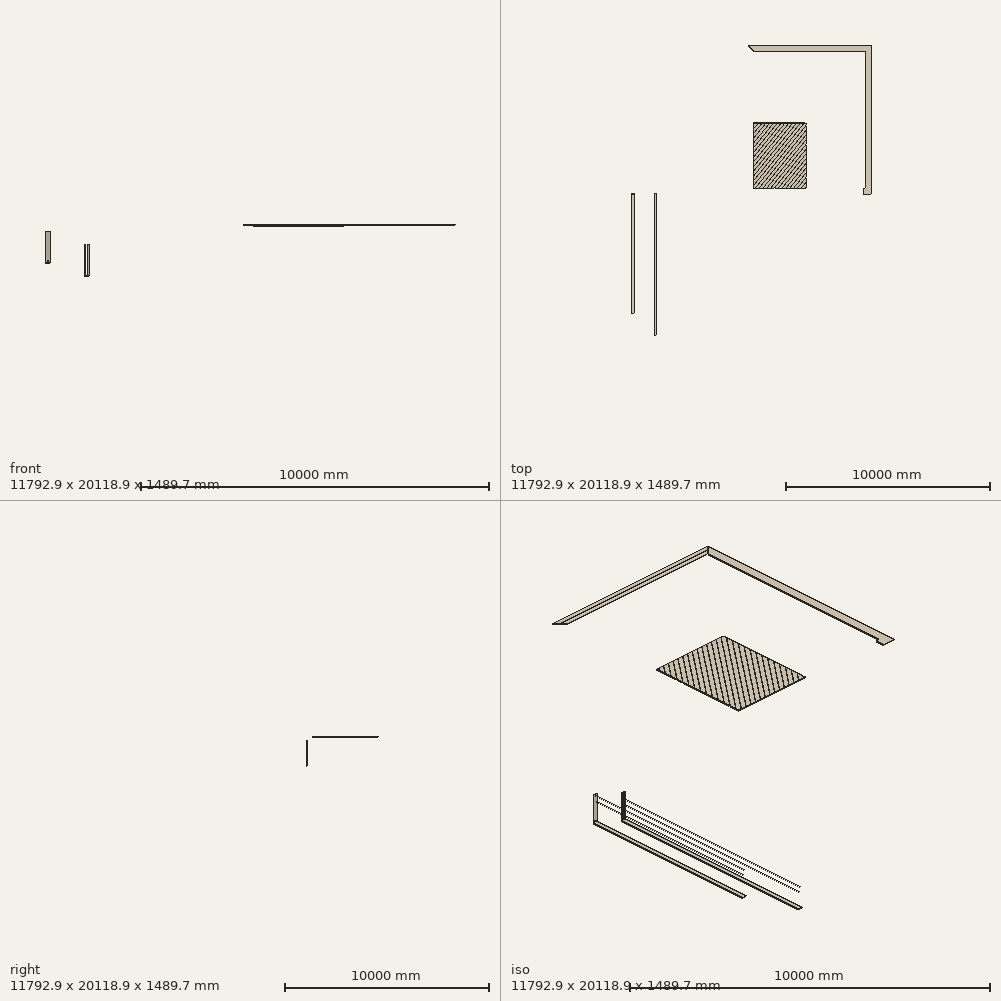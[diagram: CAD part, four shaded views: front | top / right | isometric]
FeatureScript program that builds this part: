
annotation { "Feature Type Name" : "Feature", "Feature Type Description" : "" }
export const myFeature = defineFeature(function(context is Context, id is Id, definition is map)
    precondition{}
    {
        {
            var Q0;
            Q0=qCreatedBy(makeId("Top.planeOp"),FACE);
            var sketch = newSketch(context, id + "F0", { "sketchPlane" : qUnion([Q0])});
            skLineSegment(sketch, "E0.bottom", {"start": v(-394.36, 7277.55) * mm, "end": v(5692.66, 7277.55) * mm});
            skLineSegment(sketch, "E0.top", {"start": v(-398.85, -37.65) * mm, "end": v(5697.15, -37.65) * mm});
            skLineSegment(sketch, "E0.left", {"start": v(-398.85, 7277.55) * mm, "end": v(-398.85, 254.45) * mm});
            skLineSegment(sketch, "E0.right", {"start": v(5697.15, 7273.06) * mm, "end": v(5697.15, -37.65) * mm});
            skLineSegment(sketch, "E1.bottom", {"start": v(5692.66, 7277.55) * mm, "end": v(5290.75, 7277.55) * mm});
            skLineSegment(sketch, "E1.left", {"start": v(5697.15, 7273.06) * mm, "end": v(5697.15, 6871.15) * mm});
            skLineSegment(sketch, "E1.right", {"start": v(5290.75, 6991.8) * mm, "end": v(5290.75, 6871.15) * mm});
            skLineSegment(sketch, "E2.bottom", {"start": v(-394.36, 7277.55) * mm, "end": v(7.55, 7277.55) * mm});
            skLineSegment(sketch, "E2.top", {"start": v(-398.85, 6871.15) * mm, "end": v(7.55, 6871.15) * mm});
            skLineSegment(sketch, "E2.left", {"start": v(-398.85, 7277.55) * mm, "end": v(-398.85, 6871.15) * mm});
            skLineSegment(sketch, "E3.left", {"start": v(5697.15, -37.65) * mm, "end": v(5697.15, 368.75) * mm});
            skLineSegment(sketch, "E3.right", {"start": v(5290.75, -37.65) * mm, "end": v(5290.75, 368.75) * mm});
            skLineSegment(sketch, "E4.bottom", {"start": v(-398.85, -37.65) * mm, "end": v(7.55, -37.65) * mm});
            skLineSegment(sketch, "E4.left", {"start": v(-398.85, 254.45) * mm, "end": v(-398.85, 368.75) * mm});
            skLineSegment(sketch, "E5", {"start": v(-398.85, 7277.55) * mm, "end": v(-259.15, 7137.85) * mm});
            skLineSegment(sketch, "E6.0", {"start": v(-398.85, 7137.85) * mm, "end": v(-259.15, 7137.85) * mm});
            skLineSegment(sketch, "E7.0", {"start": v(5557.45, 7116.26) * mm, "end": v(5557.45, 106.54) * mm});
            skLineSegment(sketch, "E8.0", {"start": v(-398.85, 7131.5) * mm, "end": v(-252.8, 7131.5) * mm});
            skLineSegment(sketch, "E9.0", {"start": v(-398.85, 6991.8) * mm, "end": v(-113.1, 6991.8) * mm});
            skLineSegment(sketch, "E10.trimOffspring", {"start": v(5411.4, 6987.31) * mm, "end": v(5411.4, 252.6) * mm});
            skLineSegment(sketch, "E11.trimOffspring", {"start": v(5551.1, 7116.26) * mm, "end": v(5551.1, 112.9) * mm});
            skLineSegment(sketch, "E12.trimOffspring", {"start": v(5411.4, 6871.15) * mm, "end": v(5290.75, 6871.15) * mm});
            skLineSegment(sketch, "E13.0", {"start": v(5692.66, 7277.55) * mm, "end": v(5552.96, 7137.85) * mm});
            skLineSegment(sketch, "E14.0", {"start": v(5697.15, 7273.06) * mm, "end": v(5557.45, 7133.36) * mm});
            skLineSegment(sketch, "E15.trimOffspring", {"start": v(5290.75, 6875.64) * mm, "end": v(5288.5, 6873.4) * mm});
            skLineSegment(sketch, "E16.trimOffspring", {"start": v(5295.24, 6871.15) * mm, "end": v(5293, 6868.9) * mm});
            skLineSegment(sketch, "E17.trimOffspring", {"start": v(5546.6, 7131.5) * mm, "end": v(5406.9, 6991.8) * mm});
            skLineSegment(sketch, "E18.trimOffspring", {"start": v(5551.1, 7127.01) * mm, "end": v(5411.4, 6987.31) * mm});
            skLineSegment(sketch, "E19.0", {"start": v(-394.36, 7277.55) * mm, "end": v(-254.66, 7137.85) * mm});
            skLineSegment(sketch, "E20.trimOffspring", {"start": v(-248.31, 7131.5) * mm, "end": v(-108.61, 6991.8) * mm});
            skLineSegment(sketch, "E21.trimOffspring", {"start": v(-252.8, 7131.5) * mm, "end": v(7.55, 6871.15) * mm});
            skLineSegment(sketch, "E22.trimOffspring", {"start": v(-254.66, 7137.85) * mm, "end": v(5536.98, 7137.85) * mm});
            skLineSegment(sketch, "E23.trimOffspring", {"start": v(-248.31, 7131.5) * mm, "end": v(5536.98, 7131.5) * mm});
            skLineSegment(sketch, "E24.trimOffspring", {"start": v(-108.61, 6991.8) * mm, "end": v(5406.9, 6991.8) * mm});
            skLineSegment(sketch, "E25.trimOffspring", {"start": v(7.55, 6875.64) * mm, "end": v(7.55, 6871.15) * mm});
            skLineSegment(sketch, "E26.trimOffspring", {"start": v(7.55, 6875.64) * mm, "end": v(9.8, 6873.4) * mm});
            skLineSegment(sketch, "E27.0", {"start": v(5697.15, -33.16) * mm, "end": v(5557.45, 106.54) * mm});
            skLineSegment(sketch, "E28.trimOffspring", {"start": v(5551.1, 112.9) * mm, "end": v(5411.4, 252.6) * mm});
            skLineSegment(sketch, "E29", {"start": v(5546.6, 7131.5) * mm, "end": v(5551.1, 7127.01) * mm});
            skLineSegment(sketch, "E30", {"start": v(5557.45, 7133.36) * mm, "end": v(5552.96, 7137.85) * mm});
            skLineSegment(sketch, "E31", {"start": v(5536.98, 7137.85) * mm, "end": v(5536.98, 7131.5) * mm});
            skLineSegment(sketch, "E32", {"start": v(5551.1, 7116.26) * mm, "end": v(5557.45, 7116.26) * mm});
            skPoint(sketch, "E33.orphan", {"position": v(5546.6, 7137.85) * mm});
            skLineSegment(sketch, "E34", {"start": v(5692.66, 7277.55) * mm, "end": v(5703.74, 7277.55) * mm});
            skLineSegment(sketch, "E35", {"start": v(5697.15, 7273.06) * mm, "end": v(5697.15, 7281.54) * mm});
            skLineSegment(sketch, "E36.0", {"start": v(-106.75, 254.45) * mm, "end": v(-16.83, 254.45) * mm});
            skLineSegment(sketch, "E37.0", {"start": v(-106.75, 7137.85) * mm, "end": v(-106.75, 7131.5) * mm});
            skLineSegment(sketch, "E38.trimOffspring", {"start": v(-106.75, 6991.8) * mm, "end": v(-106.75, 6871.15) * mm});
            skLineSegment(sketch, "E39.trimOffspring", {"start": v(5551.1, 254.45) * mm, "end": v(5557.45, 254.45) * mm});
            skLineSegment(sketch, "E40", {"start": v(2506.27, 254.45) * mm, "end": v(2506.27, 3473.9) * mm});
            skLineSegment(sketch, "E41", {"start": v(-106.75, 3477.08) * mm, "end": v(1529.62, 3477.08) * mm});
            skLineSegment(sketch, "E42.0", {"start": v(-16.83, 254.45) * mm, "end": v(2506.27, 3366.17) * mm});
            skLineSegment(sketch, "E43.0", {"start": v(-106.75, 365.36) * mm, "end": v(2416.35, 3477.08) * mm});
            skLineSegment(sketch, "E44.0", {"start": v(-106.75, 375.44) * mm, "end": v(2408.17, 3477.08) * mm});
            skLineSegment(sketch, "E45.0", {"start": v(-274.45, 390.43) * mm, "end": v(-271.21, 394.43) * mm});
            skLineSegment(sketch, "E46.0", {"start": v(-106.75, 607.34) * mm, "end": v(2220.14, 3477.08) * mm});
            skLineSegment(sketch, "E47.0.1.0", {"start": v(-106.75, 829.06) * mm, "end": v(2040.36, 3477.08) * mm});
            skLineSegment(sketch, "E47.0.1.1", {"start": v(-106.75, 839.14) * mm, "end": v(2032.18, 3477.08) * mm});
            skLineSegment(sketch, "E47.0.2.0", {"start": v(-496.25, 580.5) * mm, "end": v(-398.85, 700.62) * mm});
            skLineSegment(sketch, "E47.0.2.1", {"start": v(-501.18, 584.5) * mm, "end": v(-398.85, 710.7) * mm});
            skLineSegment(sketch, "E47.0.3.0", {"start": v(-607.15, 675.55) * mm, "end": v(-398.85, 932.43) * mm});
            skLineSegment(sketch, "E47.0.3.1", {"start": v(-612.08, 679.55) * mm, "end": v(-398.85, 942.51) * mm});
            skLineSegment(sketch, "E47.0.4.0", {"start": v(-718.04, 770.58) * mm, "end": v(-398.85, 1164.24) * mm});
            skLineSegment(sketch, "E47.0.4.1", {"start": v(-722.98, 774.58) * mm, "end": v(-398.85, 1174.32) * mm});
            skLineSegment(sketch, "E47.0.5.0", {"start": v(-828.94, 865.62) * mm, "end": v(-398.85, 1396.05) * mm});
            skLineSegment(sketch, "E47.0.5.1", {"start": v(-833.87, 869.62) * mm, "end": v(-398.85, 1406.13) * mm});
            skLineSegment(sketch, "E47.0.6.0", {"start": v(-939.84, 960.66) * mm, "end": v(-398.85, 1627.85) * mm});
            skLineSegment(sketch, "E47.0.6.1", {"start": v(-944.77, 964.66) * mm, "end": v(-398.85, 1637.94) * mm});
            skLineSegment(sketch, "E47.0.7.0", {"start": v(-1050.74, 1055.7) * mm, "end": v(-398.85, 1859.66) * mm});
            skLineSegment(sketch, "E47.0.7.1", {"start": v(-1055.67, 1059.7) * mm, "end": v(-398.85, 1869.74) * mm});
            skLineSegment(sketch, "E47.0.8.0", {"start": v(-1161.63, 1150.74) * mm, "end": v(-398.85, 2091.47) * mm});
            skLineSegment(sketch, "E47.0.8.1", {"start": v(-1166.57, 1154.74) * mm, "end": v(-398.85, 2101.55) * mm});
            skLineSegment(sketch, "E47.0.9.0", {"start": v(-1272.53, 1245.78) * mm, "end": v(-398.85, 2323.28) * mm});
            skLineSegment(sketch, "E47.0.9.1", {"start": v(-1277.46, 1249.78) * mm, "end": v(-398.85, 2333.36) * mm});
            skLineSegment(sketch, "E47.0.10.0", {"start": v(-1383.43, 1340.81) * mm, "end": v(-398.85, 2555.09) * mm});
            skLineSegment(sketch, "E47.0.10.1", {"start": v(-1388.36, 1344.81) * mm, "end": v(-398.85, 2565.17) * mm});
            skLineSegment(sketch, "E47.0.11.0", {"start": v(-1494.33, 1435.85) * mm, "end": v(-398.85, 2786.9) * mm});
            skLineSegment(sketch, "E47.0.11.1", {"start": v(-1499.26, 1439.85) * mm, "end": v(-398.85, 2796.98) * mm});
            skLineSegment(sketch, "E47.0.12.0", {"start": v(-1605.23, 1530.9) * mm, "end": v(-398.85, 3018.7) * mm});
            skLineSegment(sketch, "E47.0.12.1", {"start": v(-1610.16, 1534.9) * mm, "end": v(-398.85, 3028.78) * mm});
            skLineSegment(sketch, "E47.direction1", {"start": v(-279.39, 394.43) * mm, "end": v(-253.99, 394.43) * mm, "construction": true});
            skLineSegment(sketch, "E47.direction2", {"start": v(-279.39, 394.43) * mm, "end": v(-390.28, 489.47) * mm, "construction": true});
            skLineSegment(sketch, "E48.0", {"start": v(-8.65, 254.45) * mm, "end": v(2506.27, 3356.1) * mm});
            skLineSegment(sketch, "E49.1.0.0", {"start": v(171, 254.45) * mm, "end": v(2506.27, 3134.52) * mm});
            skLineSegment(sketch, "E49.1.0.1", {"start": v(179.18, 254.45) * mm, "end": v(2506.27, 3124.44) * mm});
            skLineSegment(sketch, "E49.2.0.0", {"start": v(358.83, 254.45) * mm, "end": v(2506.27, 2902.87) * mm});
            skLineSegment(sketch, "E49.2.0.1", {"start": v(367, 254.45) * mm, "end": v(2506.27, 2892.8) * mm});
            skLineSegment(sketch, "E49.3.0.0", {"start": v(274.82, -80.8) * mm, "end": v(309.82, -37.65) * mm});
            skLineSegment(sketch, "E49.3.0.1", {"start": v(279.75, -84.8) * mm, "end": v(318, -37.65) * mm});
            skLineSegment(sketch, "E49.4.0.0", {"start": v(383.93, -177.9) * mm, "end": v(497.65, -37.65) * mm});
            skLineSegment(sketch, "E49.4.0.1", {"start": v(388.86, -181.9) * mm, "end": v(505.82, -37.65) * mm});
            skLineSegment(sketch, "E49.5.0.0", {"start": v(493.04, -274.99) * mm, "end": v(685.48, -37.65) * mm});
            skLineSegment(sketch, "E49.5.0.1", {"start": v(497.97, -278.99) * mm, "end": v(693.65, -37.65) * mm});
            skLineSegment(sketch, "E49.6.0.0", {"start": v(602.14, -372.08) * mm, "end": v(873.3, -37.65) * mm});
            skLineSegment(sketch, "E49.6.0.1", {"start": v(607.07, -376.07) * mm, "end": v(881.48, -37.65) * mm});
            skLineSegment(sketch, "E49.7.0.0", {"start": v(711.25, -469.17) * mm, "end": v(1061.14, -37.65) * mm});
            skLineSegment(sketch, "E49.7.0.1", {"start": v(716.18, -473.16) * mm, "end": v(1069.31, -37.65) * mm});
            skLineSegment(sketch, "E49.8.0.0", {"start": v(820.35, -566.25) * mm, "end": v(1248.97, -37.65) * mm});
            skLineSegment(sketch, "E49.8.0.1", {"start": v(825.29, -570.25) * mm, "end": v(1257.15, -37.65) * mm});
            skLineSegment(sketch, "E49.9.0.0", {"start": v(929.46, -663.34) * mm, "end": v(1436.8, -37.65) * mm});
            skLineSegment(sketch, "E49.9.0.1", {"start": v(934.4, -667.34) * mm, "end": v(1444.98, -37.65) * mm});
            skLineSegment(sketch, "E49.10.0.0", {"start": v(1038.57, -760.43) * mm, "end": v(1624.63, -37.65) * mm});
            skLineSegment(sketch, "E49.10.0.1", {"start": v(1043.5, -764.43) * mm, "end": v(1632.8, -37.65) * mm});
            skLineSegment(sketch, "E49.11.0.0", {"start": v(1147.67, -857.52) * mm, "end": v(1812.46, -37.65) * mm});
            skLineSegment(sketch, "E49.11.0.1", {"start": v(1152.6, -861.52) * mm, "end": v(1820.64, -37.65) * mm});
            skLineSegment(sketch, "E49.12.0.0", {"start": v(1256.78, -954.61) * mm, "end": v(2000.3, -37.65) * mm});
            skLineSegment(sketch, "E49.12.0.1", {"start": v(1261.71, -958.61) * mm, "end": v(2008.47, -37.65) * mm});
            skLineSegment(sketch, "E49.direction1", {"start": v(-52.5, 210.46) * mm, "end": v(56.6, 113.37) * mm, "construction": true});
            skLineSegment(sketch, "E50.0.13.0", {"start": v(1365.89, -1051.7) * mm, "end": v(2188.12, -37.65) * mm});
            skLineSegment(sketch, "E50.3.13.0", {"start": v(1370.82, -1055.7) * mm, "end": v(2196.3, -37.65) * mm});
            skPoint(sketch, "E51.orphan", {"position": v(3760.7, 2365.1) * mm});
            skPoint(sketch, "E52.orphan", {"position": v(3983.84, 2166.92) * mm});
            skPoint(sketch, "E53.orphan", {"position": v(3978.91, 2170.92) * mm});
            skPoint(sketch, "E54.orphan", {"position": v(3874.74, 2264.01) * mm});
            skPoint(sketch, "E55.orphan", {"position": v(3869.8, 2268.01) * mm});
            skPoint(sketch, "E56.orphan", {"position": v(3765.63, 2361.1) * mm});
            skPoint(sketch, "E57.orphan", {"position": v(3656.53, 2458.2) * mm});
            skPoint(sketch, "E58.orphan", {"position": v(3651.6, 2462.2) * mm});
            skPoint(sketch, "E59.orphan", {"position": v(3547.42, 2555.28) * mm});
            skPoint(sketch, "E60.orphan", {"position": v(3542.49, 2559.28) * mm});
            skPoint(sketch, "E61.orphan", {"position": v(3438.31, 2652.37) * mm});
            skPoint(sketch, "E62.orphan", {"position": v(3433.38, 2656.37) * mm});
            skPoint(sketch, "E63.orphan", {"position": v(3329.2, 2749.46) * mm});
            skPoint(sketch, "E64.orphan", {"position": v(3324.27, 2753.46) * mm});
            skPoint(sketch, "E65.orphan", {"position": v(3220.1, 2846.55) * mm});
            skPoint(sketch, "E66.orphan", {"position": v(3215.17, 2850.55) * mm});
            skPoint(sketch, "E67.orphan", {"position": v(3111, 2943.64) * mm});
            skPoint(sketch, "E68.orphan", {"position": v(3106.06, 2947.64) * mm});
            skPoint(sketch, "E69.orphan", {"position": v(3001.89, 3040.73) * mm});
            skPoint(sketch, "E70.orphan", {"position": v(2996.95, 3044.73) * mm});
            skPoint(sketch, "E71.orphan", {"position": v(2887.85, 3141.82) * mm});
            skPoint(sketch, "E72.orphan", {"position": v(2892.78, 3137.82) * mm});
            skPoint(sketch, "E73.orphan", {"position": v(2778.74, 3238.9) * mm});
            skPoint(sketch, "E74.orphan", {"position": v(2783.67, 3234.9) * mm});
            skPoint(sketch, "E75.orphan", {"position": v(2669.63, 3336) * mm});
            skPoint(sketch, "E76.orphan", {"position": v(2674.57, 3332) * mm});
            skPoint(sketch, "E77.orphan", {"position": v(2565.46, 3429.09) * mm});
            skPoint(sketch, "E78.orphan", {"position": v(2560.53, 3433.09) * mm});
            skPoint(sketch, "E79.orphan", {"position": v(2338.57, 3613.06) * mm});
            skPoint(sketch, "E80.orphan", {"position": v(2333.64, 3617.05) * mm});
            skPoint(sketch, "E81.orphan", {"position": v(2222.74, 3712.1) * mm});
            skPoint(sketch, "E82.orphan", {"position": v(2227.67, 3708.1) * mm});
            skPoint(sketch, "E83.orphan", {"position": v(2111.84, 3807.13) * mm});
            skPoint(sketch, "E84.orphan", {"position": v(2116.78, 3803.13) * mm});
            skPoint(sketch, "E85.orphan", {"position": v(2005.88, 3898.17) * mm});
            skPoint(sketch, "E86.orphan", {"position": v(2000.95, 3902.17) * mm});
            skPoint(sketch, "E87.orphan", {"position": v(1894.98, 3993.2) * mm});
            skPoint(sketch, "E88.orphan", {"position": v(1890.05, 3997.2) * mm});
            skPoint(sketch, "E89.orphan", {"position": v(1784.08, 4088.25) * mm});
            skLineSegment(sketch, "E90", {"start": v(1529.62, 3477.08) * mm, "end": v(2506.27, 3477.08) * mm});
            skPoint(sketch, "E91.orphan", {"position": v(1779.15, 4092.25) * mm});
            skPoint(sketch, "E92.orphan", {"position": v(1673.19, 4183.29) * mm});
            skPoint(sketch, "E93.orphan", {"position": v(1668.25, 4187.29) * mm});
            skPoint(sketch, "E94.orphan", {"position": v(1562.29, 4278.32) * mm});
            skPoint(sketch, "E95.orphan", {"position": v(1557.36, 4282.32) * mm});
            skPoint(sketch, "E96.orphan", {"position": v(1451.4, 4373.36) * mm});
            skPoint(sketch, "E97.orphan", {"position": v(1446.46, 4377.36) * mm});
            skPoint(sketch, "E98.orphan", {"position": v(1340.5, 4468.4) * mm});
            skPoint(sketch, "E99.orphan", {"position": v(1335.56, 4472.4) * mm});
            skPoint(sketch, "E100.orphan", {"position": v(1229.6, 4563.44) * mm});
            skPoint(sketch, "E101.orphan", {"position": v(1224.66, 4567.44) * mm});
            skPoint(sketch, "E102.orphan", {"position": v(1118.7, 4658.48) * mm});
            skPoint(sketch, "E103.orphan", {"position": v(1113.76, 4662.48) * mm});
            skPoint(sketch, "E104.orphan", {"position": v(1007.8, 4753.52) * mm});
            skPoint(sketch, "E105.orphan", {"position": v(1002.87, 4757.52) * mm});
            skLineSegment(sketch, "E106.trimOffspring", {"start": v(-106.75, 3389.03) * mm, "end": v(-35.36, 3477.08) * mm});
            skLineSegment(sketch, "E107.trimOffspring", {"start": v(-106.75, 3378.95) * mm, "end": v(-27.18, 3477.08) * mm});
            skLineSegment(sketch, "E108.trimOffspring", {"start": v(-106.75, 3157.22) * mm, "end": v(152.6, 3477.08) * mm});
            skLineSegment(sketch, "E109.trimOffspring", {"start": v(-106.75, 3147.14) * mm, "end": v(160.77, 3477.08) * mm});
            skLineSegment(sketch, "E110.trimOffspring", {"start": v(-106.75, 2925.41) * mm, "end": v(340.56, 3477.08) * mm});
            skLineSegment(sketch, "E111.trimOffspring", {"start": v(-106.75, 2915.33) * mm, "end": v(348.73, 3477.08) * mm});
            skLineSegment(sketch, "E112.trimOffspring", {"start": v(-106.75, 2693.6) * mm, "end": v(528.52, 3477.08) * mm});
            skLineSegment(sketch, "E113.trimOffspring", {"start": v(-106.75, 2683.52) * mm, "end": v(536.7, 3477.08) * mm});
            skLineSegment(sketch, "E114.trimOffspring", {"start": v(-106.75, 2461.8) * mm, "end": v(716.47, 3477.08) * mm});
            skLineSegment(sketch, "E115.trimOffspring", {"start": v(-106.75, 2451.72) * mm, "end": v(724.65, 3477.08) * mm});
            skLineSegment(sketch, "E116.trimOffspring", {"start": v(-106.75, 2229.99) * mm, "end": v(904.43, 3477.08) * mm});
            skLineSegment(sketch, "E117.trimOffspring", {"start": v(-106.75, 2219.9) * mm, "end": v(912.6, 3477.08) * mm});
            skLineSegment(sketch, "E118.trimOffspring", {"start": v(-106.75, 1998.18) * mm, "end": v(1092.4, 3477.08) * mm});
            skLineSegment(sketch, "E119.trimOffspring", {"start": v(-106.75, 1988.1) * mm, "end": v(1100.57, 3477.08) * mm});
            skLineSegment(sketch, "E120.trimOffspring", {"start": v(-106.75, 1766.37) * mm, "end": v(1280.35, 3477.08) * mm});
            skLineSegment(sketch, "E121.trimOffspring", {"start": v(-106.75, 1756.3) * mm, "end": v(1288.52, 3477.08) * mm});
            skLineSegment(sketch, "E122.trimOffspring", {"start": v(-106.75, 1524.48) * mm, "end": v(1476.48, 3477.08) * mm});
            skLineSegment(sketch, "E123.trimOffspring", {"start": v(-106.75, 1534.57) * mm, "end": v(1468.3, 3477.08) * mm});
            skLineSegment(sketch, "E124.trimOffspring", {"start": v(-106.75, 1302.76) * mm, "end": v(1656.27, 3477.08) * mm});
            skLineSegment(sketch, "E125.trimOffspring", {"start": v(-106.75, 1292.68) * mm, "end": v(1664.44, 3477.08) * mm});
            skLineSegment(sketch, "E126.trimOffspring", {"start": v(-106.75, 1070.95) * mm, "end": v(1844.23, 3477.08) * mm});
            skLineSegment(sketch, "E127.trimOffspring", {"start": v(-106.75, 1060.87) * mm, "end": v(1852.4, 3477.08) * mm});
            skPoint(sketch, "E128.orphan", {"position": v(-385.35, 485.47) * mm});
            skLineSegment(sketch, "E129.trimOffspring", {"start": v(-106.75, 597.25) * mm, "end": v(2228.32, 3477.08) * mm});
            skPoint(sketch, "E130.orphan", {"position": v(-47.57, 206.46) * mm});
            skPoint(sketch, "E131.orphan", {"position": v(61.54, 109.37) * mm});
            skPoint(sketch, "E132.orphan", {"position": v(165.72, 16.28) * mm});
            skPoint(sketch, "E133.orphan", {"position": v(170.65, 12.28) * mm});
            skLineSegment(sketch, "E134.trimOffspring", {"start": v(554.84, 254.45) * mm, "end": v(2506.27, 2661.14) * mm});
            skLineSegment(sketch, "E135.trimOffspring", {"start": v(546.66, 254.45) * mm, "end": v(2506.27, 2671.22) * mm});
            skLineSegment(sketch, "E136.trimOffspring", {"start": v(734.5, 254.45) * mm, "end": v(2506.27, 2439.57) * mm});
            skLineSegment(sketch, "E137.trimOffspring", {"start": v(742.67, 254.45) * mm, "end": v(2506.27, 2429.5) * mm});
            skLineSegment(sketch, "E138.trimOffspring", {"start": v(922.32, 254.45) * mm, "end": v(2506.27, 2207.92) * mm});
            skLineSegment(sketch, "E139.trimOffspring", {"start": v(930.5, 254.45) * mm, "end": v(2506.27, 2197.84) * mm});
            skLineSegment(sketch, "E140.trimOffspring", {"start": v(1110.15, 254.45) * mm, "end": v(2506.27, 1976.27) * mm});
            skLineSegment(sketch, "E141.trimOffspring", {"start": v(1118.33, 254.45) * mm, "end": v(2506.27, 1966.2) * mm});
            skLineSegment(sketch, "E142.trimOffspring", {"start": v(1297.99, 254.45) * mm, "end": v(2506.27, 1744.62) * mm});
            skLineSegment(sketch, "E143.trimOffspring", {"start": v(1306.16, 254.45) * mm, "end": v(2506.27, 1734.54) * mm});
            skLineSegment(sketch, "E144.trimOffspring", {"start": v(1494, 254.45) * mm, "end": v(2506.27, 1502.9) * mm});
            skLineSegment(sketch, "E145.trimOffspring", {"start": v(1485.82, 254.45) * mm, "end": v(2506.27, 1512.97) * mm});
            skLineSegment(sketch, "E146.trimOffspring", {"start": v(1681.82, 254.45) * mm, "end": v(2506.27, 1271.24) * mm});
            skLineSegment(sketch, "E147.trimOffspring", {"start": v(1673.65, 254.45) * mm, "end": v(2506.27, 1281.32) * mm});
            skLineSegment(sketch, "E148.trimOffspring", {"start": v(1869.65, 254.45) * mm, "end": v(2506.27, 1039.6) * mm});
            skLineSegment(sketch, "E149.trimOffspring", {"start": v(1861.48, 254.45) * mm, "end": v(2506.27, 1049.68) * mm});
            skLineSegment(sketch, "E150.trimOffspring", {"start": v(2057.48, 254.45) * mm, "end": v(2506.27, 807.94) * mm});
            skLineSegment(sketch, "E151.trimOffspring", {"start": v(2049.3, 254.45) * mm, "end": v(2506.27, 818.03) * mm});
            skLineSegment(sketch, "E152.trimOffspring", {"start": v(2237.14, 254.45) * mm, "end": v(2506.27, 586.38) * mm});
            skLineSegment(sketch, "E153.trimOffspring", {"start": v(2245.31, 254.45) * mm, "end": v(2506.27, 576.3) * mm});
            skLineSegment(sketch, "E154.trimOffspring", {"start": v(2424.97, 254.45) * mm, "end": v(2506.27, 354.73) * mm});
            skLineSegment(sketch, "E155.trimOffspring", {"start": v(2433.14, 254.45) * mm, "end": v(2506.27, 344.64) * mm});
            skLineSegment(sketch, "E156.0", {"start": v(2509.45, 254.45) * mm, "end": v(2509.45, 3477.08) * mm});
            skLineSegment(sketch, "E157.0", {"start": v(-106.75, 3473.9) * mm, "end": v(1529.62, 3473.9) * mm});
            skLineSegment(sketch, "E158.0", {"start": v(1529.62, 3473.9) * mm, "end": v(2506.27, 3473.9) * mm});
            skLineSegment(sketch, "E159.trimOffspring", {"start": v(2433.14, 254.45) * mm, "end": v(5411.4, 254.45) * mm});
            skLineSegment(sketch, "E160.trimOffspring", {"start": v(2245.31, 254.45) * mm, "end": v(2424.97, 254.45) * mm});
            skLineSegment(sketch, "E161.trimOffspring", {"start": v(1869.65, 254.45) * mm, "end": v(2049.3, 254.45) * mm});
            skLineSegment(sketch, "E162.trimOffspring", {"start": v(1681.82, 254.45) * mm, "end": v(1861.48, 254.45) * mm});
            skLineSegment(sketch, "E163", {"start": v(2057.48, 254.45) * mm, "end": v(2237.14, 254.45) * mm});
            skLineSegment(sketch, "E164.trimOffspring", {"start": v(1494, 254.45) * mm, "end": v(1673.65, 254.45) * mm});
            skLineSegment(sketch, "E165.trimOffspring", {"start": v(1306.16, 254.45) * mm, "end": v(1485.82, 254.45) * mm});
            skLineSegment(sketch, "E166.trimOffspring", {"start": v(1118.33, 254.45) * mm, "end": v(1297.99, 254.45) * mm});
            skLineSegment(sketch, "E167.trimOffspring", {"start": v(930.5, 254.45) * mm, "end": v(1110.15, 254.45) * mm});
            skLineSegment(sketch, "E168.trimOffspring", {"start": v(742.67, 254.45) * mm, "end": v(922.32, 254.45) * mm});
            skLineSegment(sketch, "E169.trimOffspring", {"start": v(554.84, 254.45) * mm, "end": v(734.5, 254.45) * mm});
            skLineSegment(sketch, "E170.trimOffspring", {"start": v(367, 254.45) * mm, "end": v(546.66, 254.45) * mm});
            skLineSegment(sketch, "E171.trimOffspring", {"start": v(179.18, 254.45) * mm, "end": v(358.83, 254.45) * mm});
            skLineSegment(sketch, "E172.trimOffspring", {"start": v(-8.65, 254.45) * mm, "end": v(171, 254.45) * mm});
            skPoint(sketch, "E173.orphan", {"position": v(-106.75, -37.65) * mm});
            skLineSegment(sketch, "E174.trimOffspring", {"start": v(-106.75, 365.36) * mm, "end": v(-106.75, 254.45) * mm});
            skLineSegment(sketch, "E175.trimOffspring", {"start": v(-106.75, 597.25) * mm, "end": v(-106.75, 375.44) * mm});
            skLineSegment(sketch, "E176.trimOffspring", {"start": v(-106.75, 829.06) * mm, "end": v(-106.75, 607.34) * mm});
            skLineSegment(sketch, "E177.trimOffspring", {"start": v(-106.75, 1060.87) * mm, "end": v(-106.75, 839.14) * mm});
            skLineSegment(sketch, "E178.trimOffspring", {"start": v(-106.75, 1292.68) * mm, "end": v(-106.75, 1070.95) * mm});
            skLineSegment(sketch, "E179.trimOffspring", {"start": v(-106.75, 1524.48) * mm, "end": v(-106.75, 1302.76) * mm});
            skLineSegment(sketch, "E180.trimOffspring", {"start": v(-106.75, 1756.3) * mm, "end": v(-106.75, 1534.57) * mm});
            skLineSegment(sketch, "E181.trimOffspring", {"start": v(-106.75, 1988.1) * mm, "end": v(-106.75, 1766.37) * mm});
            skLineSegment(sketch, "E182.trimOffspring", {"start": v(-106.75, 2219.9) * mm, "end": v(-106.75, 1998.18) * mm});
            skLineSegment(sketch, "E183.trimOffspring", {"start": v(-106.75, 2451.72) * mm, "end": v(-106.75, 2229.99) * mm});
            skLineSegment(sketch, "E184.trimOffspring", {"start": v(-106.75, 2683.52) * mm, "end": v(-106.75, 2461.8) * mm});
            skLineSegment(sketch, "E185.trimOffspring", {"start": v(-106.75, 2915.33) * mm, "end": v(-106.75, 2693.6) * mm});
            skLineSegment(sketch, "E186.trimOffspring", {"start": v(-106.75, 3147.14) * mm, "end": v(-106.75, 2925.41) * mm});
            skLineSegment(sketch, "E187.trimOffspring", {"start": v(-106.75, 3378.95) * mm, "end": v(-106.75, 3157.22) * mm});
            skLineSegment(sketch, "E188.trimOffspring", {"start": v(-106.75, 3477.08) * mm, "end": v(-106.75, 3389.03) * mm});
            skLineSegment(sketch, "E189", {"start": v(2506.27, 3477.08) * mm, "end": v(2509.45, 3477.08) * mm});
            skPoint(sketch, "E190.orphan", {"position": v(2506.27, 4118.32) * mm});
            skLineSegment(sketch, "E191.0", {"start": v(2433.14, 111.58) * mm, "end": v(5411.4, 111.58) * mm});
            skSolve(sketch);
        }
        {
            var Q0;
            {var subQ3=sQuery(id+"F0.wireOp",EDGE,"E17.trimOffspring");Q0=makeQuery(id+"F0.imprint","IMPRINT",FACE,{"disambiguationData":[TD([[makeQuery(id+"F0.imprint","IMPRINT",EDGE,{"derivedFrom":subQ3}),-1.0]])]});}
            var Q1;
            Q1=makeQuery(id+"F0.imprint","IMPRINT",FACE,{"disambiguationData":[TD([[makeQuery(id+"F0.imprint","IMPRINT",EDGE,{"derivedFrom":sQuery(id+"F0.wireOp",EDGE,"E0.bottom")}),-1.0]])]});
            var Q2;
            {var subQ1=sQuery(id+"F0.wireOp",EDGE,"E0.right");Q2=makeQuery(id+"F0.imprint","IMPRINT",FACE,{"disambiguationData":[TD([[makeQuery(id+"F0.imprint","IMPRINT",EDGE,{"derivedFrom":subQ1}),-1.0]])]});}
            var Q3;
            Q3=makeQuery(id+"F0.imprint","IMPRINT",FACE,{"disambiguationData":[TD([[makeQuery(id+"F0.imprint","IMPRINT",EDGE,{"derivedFrom":sQuery(id+"F0.wireOp",EDGE,"E11.trimOffspring")}),-1.0]])]});
            extrude(context, id + "F1", {"entities" : qUnion([Q0, Q1, Q2, Q3]), "depth" : 25.4 * mm});
        }
        {
            var Q0;
            Q0=makeQuery(id+"F1.opExtrude","CAP_FACE",FACE,{"disambiguationData":[OSD([sQuery(id+"F0.wireOp",EDGE,"E0.bottom"),sQuery(id+"F0.wireOp",EDGE,"E0.right"),sQuery(id+"F0.wireOp",EDGE,"E1.bottom"),sQuery(id+"F0.wireOp",EDGE,"E1.left"),sQuery(id+"F0.wireOp",EDGE,"E2.bottom"),sQuery(id+"F0.wireOp",EDGE,"E3.left"),sQuery(id+"F0.wireOp",EDGE,"E7.0"),sQuery(id+"F0.wireOp",EDGE,"E10.trimOffspring"),sQuery(id+"F0.wireOp",EDGE,"E11.trimOffspring"),sQuery(id+"F0.wireOp",EDGE,"E13.0"),sQuery(id+"F0.wireOp",EDGE,"E14.0"),sQuery(id+"F0.wireOp",EDGE,"E17.trimOffspring"),sQuery(id+"F0.wireOp",EDGE,"E18.trimOffspring"),sQuery(id+"F0.wireOp",EDGE,"E19.0"),sQuery(id+"F0.wireOp",EDGE,"E20.trimOffspring"),sQuery(id+"F0.wireOp",EDGE,"E22.trimOffspring"),sQuery(id+"F0.wireOp",EDGE,"E23.trimOffspring"),sQuery(id+"F0.wireOp",EDGE,"E24.trimOffspring"),sQuery(id+"F0.wireOp",EDGE,"E27.0"),sQuery(id+"F0.wireOp",EDGE,"E28.trimOffspring"),sQuery(id+"F0.wireOp",EDGE,"E29"),sQuery(id+"F0.wireOp",EDGE,"E30"),sQuery(id+"F0.wireOp",EDGE,"E31"),sQuery(id+"F0.wireOp",EDGE,"E32")])],"isStart":false});
            extrude(context, id + "F2", {"entities" : qUnion([Q0]), "depth" : 25.4 * mm});
        }
        {
            var Q0;
            Q0=makeQuery(id+"F1.opExtrude","SWEPT_BODY",BODY,{"disambiguationData":[OSD([sQuery(id+"F0.wireOp",EDGE,"E0.bottom"),sQuery(id+"F0.wireOp",EDGE,"E0.right"),sQuery(id+"F0.wireOp",EDGE,"E1.bottom"),sQuery(id+"F0.wireOp",EDGE,"E1.left"),sQuery(id+"F0.wireOp",EDGE,"E2.bottom"),sQuery(id+"F0.wireOp",EDGE,"E3.left"),sQuery(id+"F0.wireOp",EDGE,"E7.0"),sQuery(id+"F0.wireOp",EDGE,"E10.trimOffspring"),sQuery(id+"F0.wireOp",EDGE,"E11.trimOffspring"),sQuery(id+"F0.wireOp",EDGE,"E13.0"),sQuery(id+"F0.wireOp",EDGE,"E14.0"),sQuery(id+"F0.wireOp",EDGE,"E17.trimOffspring"),sQuery(id+"F0.wireOp",EDGE,"E18.trimOffspring"),sQuery(id+"F0.wireOp",EDGE,"E19.0"),sQuery(id+"F0.wireOp",EDGE,"E20.trimOffspring"),sQuery(id+"F0.wireOp",EDGE,"E22.trimOffspring"),sQuery(id+"F0.wireOp",EDGE,"E23.trimOffspring"),sQuery(id+"F0.wireOp",EDGE,"E24.trimOffspring"),sQuery(id+"F0.wireOp",EDGE,"E27.0"),sQuery(id+"F0.wireOp",EDGE,"E28.trimOffspring"),sQuery(id+"F0.wireOp",EDGE,"E29"),sQuery(id+"F0.wireOp",EDGE,"E30"),sQuery(id+"F0.wireOp",EDGE,"E31"),sQuery(id+"F0.wireOp",EDGE,"E32")])]});
            deleteBodies(context, id + "F3", {"entities" : qUnion([Q0])});
        }
        {
            var Q0;
            {var subQ0=sQuery(id+"F0.wireOp",EDGE,"E175.trimOffspring");Q0=makeQuery(id+"F0.imprint","IMPRINT",FACE,{"disambiguationData":[TD([[makeQuery(id+"F0.imprint","IMPRINT",EDGE,{"derivedFrom":subQ0}),1.0]])]});}
            var Q1;
            {var subQ0=sQuery(id+"F0.wireOp",EDGE,"E143.trimOffspring");Q1=makeQuery(id+"F0.imprint","IMPRINT",FACE,{"disambiguationData":[TD([[makeQuery(id+"F0.imprint","IMPRINT",EDGE,{"derivedFrom":subQ0}),-1.0]])]});}
            var Q2;
            {var subQ0=sQuery(id+"F0.wireOp",EDGE,"E134.trimOffspring");Q2=makeQuery(id+"F0.imprint","IMPRINT",FACE,{"disambiguationData":[TD([[makeQuery(id+"F0.imprint","IMPRINT",EDGE,{"derivedFrom":subQ0}),-1.0]])]});}
            var Q3;
            {var subQ0=sQuery(id+"F0.wireOp",EDGE,"E186.trimOffspring");Q3=makeQuery(id+"F0.imprint","IMPRINT",FACE,{"disambiguationData":[TD([[makeQuery(id+"F0.imprint","IMPRINT",EDGE,{"derivedFrom":subQ0}),1.0]])]});}
            var Q4;
            {var subQ7=sQuery(id+"F0.wireOp",EDGE,"E179.trimOffspring");Q4=makeQuery(id+"F0.imprint","IMPRINT",FACE,{"disambiguationData":[TD([[makeQuery(id+"F0.imprint","IMPRINT",EDGE,{"derivedFrom":subQ7}),1.0]])]});}
            var Q5;
            {var subQ0=sQuery(id+"F0.wireOp",EDGE,"E153.trimOffspring");Q5=makeQuery(id+"F0.imprint","IMPRINT",FACE,{"disambiguationData":[TD([[makeQuery(id+"F0.imprint","IMPRINT",EDGE,{"derivedFrom":subQ0}),-1.0]])]});}
            var Q6;
            {var subQ0=sQuery(id+"F0.wireOp",EDGE,"E137.trimOffspring");Q6=makeQuery(id+"F0.imprint","IMPRINT",FACE,{"disambiguationData":[TD([[makeQuery(id+"F0.imprint","IMPRINT",EDGE,{"derivedFrom":subQ0}),-1.0]])]});}
            var Q7;
            {var subQ0=sQuery(id+"F0.wireOp",EDGE,"E182.trimOffspring");Q7=makeQuery(id+"F0.imprint","IMPRINT",FACE,{"disambiguationData":[TD([[makeQuery(id+"F0.imprint","IMPRINT",EDGE,{"derivedFrom":subQ0}),1.0]])]});}
            var Q8;
            {var subQ0=sQuery(id+"F0.wireOp",EDGE,"E178.trimOffspring");Q8=makeQuery(id+"F0.imprint","IMPRINT",FACE,{"disambiguationData":[TD([[makeQuery(id+"F0.imprint","IMPRINT",EDGE,{"derivedFrom":subQ0}),1.0]])]});}
            var Q9;
            {var subQ0=sQuery(id+"F0.wireOp",EDGE,"E150.trimOffspring");Q9=makeQuery(id+"F0.imprint","IMPRINT",FACE,{"disambiguationData":[TD([[makeQuery(id+"F0.imprint","IMPRINT",EDGE,{"derivedFrom":subQ0}),-1.0]])]});}
            var Q10;
            {var subQ0=sQuery(id+"F0.wireOp",EDGE,"E184.trimOffspring");Q10=makeQuery(id+"F0.imprint","IMPRINT",FACE,{"disambiguationData":[TD([[makeQuery(id+"F0.imprint","IMPRINT",EDGE,{"derivedFrom":subQ0}),1.0]])]});}
            var Q11;
            {var subQ0=sQuery(id+"F0.wireOp",EDGE,"E139.trimOffspring");Q11=makeQuery(id+"F0.imprint","IMPRINT",FACE,{"disambiguationData":[TD([[makeQuery(id+"F0.imprint","IMPRINT",EDGE,{"derivedFrom":subQ0}),-1.0]])]});}
            var Q12;
            {var subQ0=sQuery(id+"F0.wireOp",EDGE,"E176.trimOffspring");Q12=makeQuery(id+"F0.imprint","IMPRINT",FACE,{"disambiguationData":[TD([[makeQuery(id+"F0.imprint","IMPRINT",EDGE,{"derivedFrom":subQ0}),1.0]])]});}
            var Q13;
            {var subQ0=sQuery(id+"F0.wireOp",EDGE,"E49.2.0.1");Q13=makeQuery(id+"F0.imprint","IMPRINT",FACE,{"disambiguationData":[TD([[makeQuery(id+"F0.imprint","IMPRINT",EDGE,{"derivedFrom":subQ0}),-1.0]])]});}
            var Q14;
            {var subQ0=sQuery(id+"F0.wireOp",EDGE,"E48.0");Q14=makeQuery(id+"F0.imprint","IMPRINT",FACE,{"disambiguationData":[TD([[makeQuery(id+"F0.imprint","IMPRINT",EDGE,{"derivedFrom":subQ0}),-1.0]])]});}
            var Q15;
            {var subQ0=sQuery(id+"F0.wireOp",EDGE,"E185.trimOffspring");Q15=makeQuery(id+"F0.imprint","IMPRINT",FACE,{"disambiguationData":[TD([[makeQuery(id+"F0.imprint","IMPRINT",EDGE,{"derivedFrom":subQ0}),1.0]])]});}
            var Q16;
            {var subQ0=sQuery(id+"F0.wireOp",EDGE,"E181.trimOffspring");Q16=makeQuery(id+"F0.imprint","IMPRINT",FACE,{"disambiguationData":[TD([[makeQuery(id+"F0.imprint","IMPRINT",EDGE,{"derivedFrom":subQ0}),1.0]])]});}
            var Q17;
            {var subQ0=sQuery(id+"F0.wireOp",EDGE,"E183.trimOffspring");Q17=makeQuery(id+"F0.imprint","IMPRINT",FACE,{"disambiguationData":[TD([[makeQuery(id+"F0.imprint","IMPRINT",EDGE,{"derivedFrom":subQ0}),1.0]])]});}
            var Q18;
            {var subQ0=sQuery(id+"F0.wireOp",EDGE,"E180.trimOffspring");Q18=makeQuery(id+"F0.imprint","IMPRINT",FACE,{"disambiguationData":[TD([[makeQuery(id+"F0.imprint","IMPRINT",EDGE,{"derivedFrom":subQ0}),1.0]])]});}
            var Q19;
            {var subQ0=sQuery(id+"F0.wireOp",EDGE,"E141.trimOffspring");Q19=makeQuery(id+"F0.imprint","IMPRINT",FACE,{"disambiguationData":[TD([[makeQuery(id+"F0.imprint","IMPRINT",EDGE,{"derivedFrom":subQ0}),-1.0]])]});}
            var Q20;
            {var subQ0=sQuery(id+"F0.wireOp",EDGE,"E146.trimOffspring");Q20=makeQuery(id+"F0.imprint","IMPRINT",FACE,{"disambiguationData":[TD([[makeQuery(id+"F0.imprint","IMPRINT",EDGE,{"derivedFrom":subQ0}),-1.0]])]});}
            var Q21;
            Q21=makeQuery(id+"F0.imprint","IMPRINT",FACE,{"disambiguationData":[TD([[makeQuery(id+"F0.imprint","IMPRINT",EDGE,{"derivedFrom":sQuery(id+"F0.wireOp",EDGE,"E36.0")}),1.0]])]});
            var Q22;
            {var subQ0=sQuery(id+"F0.wireOp",EDGE,"E148.trimOffspring");Q22=makeQuery(id+"F0.imprint","IMPRINT",FACE,{"disambiguationData":[TD([[makeQuery(id+"F0.imprint","IMPRINT",EDGE,{"derivedFrom":subQ0}),-1.0]])]});}
            var Q23;
            {var subQ0=sQuery(id+"F0.wireOp",EDGE,"E144.trimOffspring");Q23=makeQuery(id+"F0.imprint","IMPRINT",FACE,{"disambiguationData":[TD([[makeQuery(id+"F0.imprint","IMPRINT",EDGE,{"derivedFrom":subQ0}),-1.0]])]});}
            var Q24;
            {var subQ0=sQuery(id+"F0.wireOp",EDGE,"E177.trimOffspring");Q24=makeQuery(id+"F0.imprint","IMPRINT",FACE,{"disambiguationData":[TD([[makeQuery(id+"F0.imprint","IMPRINT",EDGE,{"derivedFrom":subQ0}),1.0]])]});}
            var Q25;
            {var subQ0=sQuery(id+"F0.wireOp",EDGE,"E187.trimOffspring");Q25=makeQuery(id+"F0.imprint","IMPRINT",FACE,{"disambiguationData":[TD([[makeQuery(id+"F0.imprint","IMPRINT",EDGE,{"derivedFrom":subQ0}),1.0]])]});}
            var Q26;
            {var subQ0=sQuery(id+"F0.wireOp",EDGE,"E49.1.0.1");Q26=makeQuery(id+"F0.imprint","IMPRINT",FACE,{"disambiguationData":[TD([[makeQuery(id+"F0.imprint","IMPRINT",EDGE,{"derivedFrom":subQ0}),-1.0]])]});}
            var Q27;
            {var subQ3=sQuery(id+"F0.wireOp",EDGE,"E155.trimOffspring");Q27=makeQuery(id+"F0.imprint","IMPRINT",FACE,{"disambiguationData":[TD([[makeQuery(id+"F0.imprint","IMPRINT",EDGE,{"derivedFrom":subQ3}),-1.0]])]});}
            var Q28;
            {var subQ0=sQuery(id+"F0.wireOp",EDGE,"E90");var subQ1=sQuery(id+"F0.wireOp",EDGE,"E47.0.1.1");var subQ2=makeQuery(id+"F0.imprint","INTERSECT",VERTEX,{"derivedFrom":[subQ1,subQ0]});Q28=makeQuery(id+"F0.imprint","IMPRINT",FACE,{"disambiguationData":[TD([[makeQuery(id+"F0.imprint","IMPRINT",EDGE,{"disambiguationData":[TD([[subQ2,1.0]])],"derivedFrom":subQ1}),1.0]])]});}
            var Q29;
            {var subQ0=sQuery(id+"F0.wireOp",EDGE,"E125.trimOffspring");var subQ1=sQuery(id+"F0.wireOp",EDGE,"E90");var subQ2=makeQuery(id+"F0.imprint","INTERSECT",VERTEX,{"derivedFrom":[subQ1,subQ0]});Q29=makeQuery(id+"F0.imprint","IMPRINT",FACE,{"disambiguationData":[TD([[makeQuery(id+"F0.imprint","IMPRINT",EDGE,{"disambiguationData":[TD([[subQ2,-1.0]])],"derivedFrom":subQ1}),-1.0]])]});}
            var Q30;
            {var subQ0=sQuery(id+"F0.wireOp",EDGE,"E90");var subQ1=sQuery(id+"F0.wireOp",EDGE,"E46.0");var subQ2=makeQuery(id+"F0.imprint","INTERSECT",VERTEX,{"derivedFrom":[subQ1,subQ0]});Q30=makeQuery(id+"F0.imprint","IMPRINT",FACE,{"disambiguationData":[TD([[makeQuery(id+"F0.imprint","IMPRINT",EDGE,{"disambiguationData":[TD([[subQ2,1.0]])],"derivedFrom":subQ1}),1.0]])]});}
            var Q31;
            {var subQ0=sQuery(id+"F0.wireOp",EDGE,"E117.trimOffspring");var subQ1=sQuery(id+"F0.wireOp",EDGE,"E41");var subQ2=makeQuery(id+"F0.imprint","INTERSECT",VERTEX,{"derivedFrom":[subQ1,subQ0]});Q31=makeQuery(id+"F0.imprint","IMPRINT",FACE,{"disambiguationData":[TD([[makeQuery(id+"F0.imprint","IMPRINT",EDGE,{"disambiguationData":[TD([[subQ2,-1.0]])],"derivedFrom":subQ1}),-1.0]])]});}
            var Q32;
            {var subQ0=sQuery(id+"F0.wireOp",EDGE,"E111.trimOffspring");var subQ1=sQuery(id+"F0.wireOp",EDGE,"E41");var subQ2=makeQuery(id+"F0.imprint","INTERSECT",VERTEX,{"derivedFrom":[subQ1,subQ0]});Q32=makeQuery(id+"F0.imprint","IMPRINT",FACE,{"disambiguationData":[TD([[makeQuery(id+"F0.imprint","IMPRINT",EDGE,{"disambiguationData":[TD([[subQ2,-1.0]])],"derivedFrom":subQ1}),-1.0]])]});}
            var Q33;
            {var subQ0=sQuery(id+"F0.wireOp",EDGE,"E90");var subQ1=sQuery(id+"F0.wireOp",EDGE,"E44.0");var subQ2=makeQuery(id+"F0.imprint","INTERSECT",VERTEX,{"derivedFrom":[subQ1,subQ0]});Q33=makeQuery(id+"F0.imprint","IMPRINT",FACE,{"disambiguationData":[TD([[makeQuery(id+"F0.imprint","IMPRINT",EDGE,{"disambiguationData":[TD([[subQ2,1.0]])],"derivedFrom":subQ1}),1.0]])]});}
            var Q34;
            {var subQ1=sQuery(id+"F0.wireOp",EDGE,"E41");var subQ5=sQuery(id+"F0.wireOp",EDGE,"E90");var subQ6=makeQuery(id+"F0.imprint","INTERSECT",VERTEX,{"derivedFrom":[subQ1,subQ5]});Q34=makeQuery(id+"F0.imprint","IMPRINT",FACE,{"disambiguationData":[TD([[makeQuery(id+"F0.imprint","IMPRINT",EDGE,{"disambiguationData":[TD([[subQ6,1.0]])],"derivedFrom":subQ1}),-1.0]])]});}
            var Q35;
            {var subQ0=sQuery(id+"F0.wireOp",EDGE,"E126.trimOffspring");var subQ1=sQuery(id+"F0.wireOp",EDGE,"E90");var subQ2=makeQuery(id+"F0.imprint","INTERSECT",VERTEX,{"derivedFrom":[subQ1,subQ0]});Q35=makeQuery(id+"F0.imprint","IMPRINT",FACE,{"disambiguationData":[TD([[makeQuery(id+"F0.imprint","IMPRINT",EDGE,{"disambiguationData":[TD([[subQ2,-1.0]])],"derivedFrom":subQ1}),-1.0]])]});}
            var Q36;
            {var subQ0=sQuery(id+"F0.wireOp",EDGE,"E113.trimOffspring");var subQ1=sQuery(id+"F0.wireOp",EDGE,"E41");var subQ2=makeQuery(id+"F0.imprint","INTERSECT",VERTEX,{"derivedFrom":[subQ1,subQ0]});Q36=makeQuery(id+"F0.imprint","IMPRINT",FACE,{"disambiguationData":[TD([[makeQuery(id+"F0.imprint","IMPRINT",EDGE,{"disambiguationData":[TD([[subQ2,-1.0]])],"derivedFrom":subQ1}),-1.0]])]});}
            var Q37;
            {var subQ0=sQuery(id+"F0.wireOp",EDGE,"E122.trimOffspring");var subQ1=sQuery(id+"F0.wireOp",EDGE,"E41");var subQ2=makeQuery(id+"F0.imprint","INTERSECT",VERTEX,{"derivedFrom":[subQ1,subQ0]});Q37=makeQuery(id+"F0.imprint","IMPRINT",FACE,{"disambiguationData":[TD([[makeQuery(id+"F0.imprint","IMPRINT",EDGE,{"disambiguationData":[TD([[subQ2,1.0]])],"derivedFrom":subQ1}),-1.0]])]});}
            var Q38;
            {var subQ0=sQuery(id+"F0.wireOp",EDGE,"E121.trimOffspring");var subQ1=sQuery(id+"F0.wireOp",EDGE,"E41");var subQ2=makeQuery(id+"F0.imprint","INTERSECT",VERTEX,{"derivedFrom":[subQ1,subQ0]});Q38=makeQuery(id+"F0.imprint","IMPRINT",FACE,{"disambiguationData":[TD([[makeQuery(id+"F0.imprint","IMPRINT",EDGE,{"disambiguationData":[TD([[subQ2,-1.0]])],"derivedFrom":subQ1}),-1.0]])]});}
            var Q39;
            {var subQ0=sQuery(id+"F0.wireOp",EDGE,"E109.trimOffspring");var subQ1=sQuery(id+"F0.wireOp",EDGE,"E41");var subQ2=makeQuery(id+"F0.imprint","INTERSECT",VERTEX,{"derivedFrom":[subQ1,subQ0]});Q39=makeQuery(id+"F0.imprint","IMPRINT",FACE,{"disambiguationData":[TD([[makeQuery(id+"F0.imprint","IMPRINT",EDGE,{"disambiguationData":[TD([[subQ2,-1.0]])],"derivedFrom":subQ1}),-1.0]])]});}
            var Q40;
            {var subQ0=sQuery(id+"F0.wireOp",EDGE,"E119.trimOffspring");var subQ1=sQuery(id+"F0.wireOp",EDGE,"E41");var subQ2=makeQuery(id+"F0.imprint","INTERSECT",VERTEX,{"derivedFrom":[subQ1,subQ0]});Q40=makeQuery(id+"F0.imprint","IMPRINT",FACE,{"disambiguationData":[TD([[makeQuery(id+"F0.imprint","IMPRINT",EDGE,{"disambiguationData":[TD([[subQ2,-1.0]])],"derivedFrom":subQ1}),-1.0]])]});}
            var Q41;
            {var subQ0=sQuery(id+"F0.wireOp",EDGE,"E107.trimOffspring");var subQ1=sQuery(id+"F0.wireOp",EDGE,"E41");var subQ2=makeQuery(id+"F0.imprint","INTERSECT",VERTEX,{"derivedFrom":[subQ1,subQ0]});Q41=makeQuery(id+"F0.imprint","IMPRINT",FACE,{"disambiguationData":[TD([[makeQuery(id+"F0.imprint","IMPRINT",EDGE,{"disambiguationData":[TD([[subQ2,-1.0]])],"derivedFrom":subQ1}),-1.0]])]});}
            var Q42;
            {var subQ0=sQuery(id+"F0.wireOp",EDGE,"E115.trimOffspring");var subQ1=sQuery(id+"F0.wireOp",EDGE,"E41");var subQ2=makeQuery(id+"F0.imprint","INTERSECT",VERTEX,{"derivedFrom":[subQ1,subQ0]});Q42=makeQuery(id+"F0.imprint","IMPRINT",FACE,{"disambiguationData":[TD([[makeQuery(id+"F0.imprint","IMPRINT",EDGE,{"disambiguationData":[TD([[subQ2,-1.0]])],"derivedFrom":subQ1}),-1.0]])]});}
            var Q43;
            {var subQ38=sQuery(id+"F0.wireOp",EDGE,"E156.0");Q43=makeQuery(id+"F0.imprint","IMPRINT",FACE,{"disambiguationData":[TD([[makeQuery(id+"F0.imprint","IMPRINT",EDGE,{"derivedFrom":subQ38}),1.0]])]});}
            var Q44;
            {var subQ0=sQuery(id+"F0.wireOp",EDGE,"E116.trimOffspring");var subQ1=sQuery(id+"F0.wireOp",EDGE,"E41");var subQ2=makeQuery(id+"F0.imprint","INTERSECT",VERTEX,{"derivedFrom":[subQ1,subQ0]});Q44=makeQuery(id+"F0.imprint","IMPRINT",FACE,{"disambiguationData":[TD([[makeQuery(id+"F0.imprint","IMPRINT",EDGE,{"disambiguationData":[TD([[subQ2,-1.0]])],"derivedFrom":subQ1}),-1.0]])]});}
            var Q45;
            {var subQ0=sQuery(id+"F0.wireOp",EDGE,"E90");var subQ1=sQuery(id+"F0.wireOp",EDGE,"E46.0");var subQ2=makeQuery(id+"F0.imprint","INTERSECT",VERTEX,{"derivedFrom":[subQ1,subQ0]});Q45=makeQuery(id+"F0.imprint","IMPRINT",FACE,{"disambiguationData":[TD([[makeQuery(id+"F0.imprint","IMPRINT",EDGE,{"disambiguationData":[TD([[subQ2,1.0]])],"derivedFrom":subQ1}),-1.0]])]});}
            var Q46;
            {var subQ0=sQuery(id+"F0.wireOp",EDGE,"E118.trimOffspring");var subQ1=sQuery(id+"F0.wireOp",EDGE,"E41");var subQ2=makeQuery(id+"F0.imprint","INTERSECT",VERTEX,{"derivedFrom":[subQ1,subQ0]});Q46=makeQuery(id+"F0.imprint","IMPRINT",FACE,{"disambiguationData":[TD([[makeQuery(id+"F0.imprint","IMPRINT",EDGE,{"disambiguationData":[TD([[subQ2,-1.0]])],"derivedFrom":subQ1}),-1.0]])]});}
            var Q47;
            {var subQ0=sQuery(id+"F0.wireOp",EDGE,"E110.trimOffspring");var subQ1=sQuery(id+"F0.wireOp",EDGE,"E41");var subQ2=makeQuery(id+"F0.imprint","INTERSECT",VERTEX,{"derivedFrom":[subQ1,subQ0]});Q47=makeQuery(id+"F0.imprint","IMPRINT",FACE,{"disambiguationData":[TD([[makeQuery(id+"F0.imprint","IMPRINT",EDGE,{"disambiguationData":[TD([[subQ2,-1.0]])],"derivedFrom":subQ1}),-1.0]])]});}
            var Q48;
            {var subQ0=sQuery(id+"F0.wireOp",EDGE,"E90");var subQ1=sQuery(id+"F0.wireOp",EDGE,"E43.0");var subQ2=makeQuery(id+"F0.imprint","INTERSECT",VERTEX,{"derivedFrom":[subQ1,subQ0]});Q48=makeQuery(id+"F0.imprint","IMPRINT",FACE,{"disambiguationData":[TD([[makeQuery(id+"F0.imprint","IMPRINT",EDGE,{"disambiguationData":[TD([[subQ2,1.0]])],"derivedFrom":subQ1}),1.0]])]});}
            var Q49;
            {var subQ0=sQuery(id+"F0.wireOp",EDGE,"E108.trimOffspring");var subQ1=sQuery(id+"F0.wireOp",EDGE,"E41");var subQ2=makeQuery(id+"F0.imprint","INTERSECT",VERTEX,{"derivedFrom":[subQ1,subQ0]});Q49=makeQuery(id+"F0.imprint","IMPRINT",FACE,{"disambiguationData":[TD([[makeQuery(id+"F0.imprint","IMPRINT",EDGE,{"disambiguationData":[TD([[subQ2,-1.0]])],"derivedFrom":subQ1}),-1.0]])]});}
            var Q50;
            {var subQ0=sQuery(id+"F0.wireOp",EDGE,"E188.trimOffspring");var subQ1=sQuery(id+"F0.wireOp",EDGE,"E41");var subQ2=makeQuery(id+"F0.imprint","INTERSECT",VERTEX,{"derivedFrom":[subQ1,subQ0]});Q50=makeQuery(id+"F0.imprint","IMPRINT",FACE,{"disambiguationData":[TD([[makeQuery(id+"F0.imprint","IMPRINT",EDGE,{"disambiguationData":[TD([[subQ2,-1.0]])],"derivedFrom":subQ1}),-1.0]])]});}
            var Q51;
            {var subQ0=sQuery(id+"F0.wireOp",EDGE,"E114.trimOffspring");var subQ1=sQuery(id+"F0.wireOp",EDGE,"E41");var subQ2=makeQuery(id+"F0.imprint","INTERSECT",VERTEX,{"derivedFrom":[subQ1,subQ0]});Q51=makeQuery(id+"F0.imprint","IMPRINT",FACE,{"disambiguationData":[TD([[makeQuery(id+"F0.imprint","IMPRINT",EDGE,{"disambiguationData":[TD([[subQ2,-1.0]])],"derivedFrom":subQ1}),-1.0]])]});}
            var Q52;
            {var subQ0=sQuery(id+"F0.wireOp",EDGE,"E90");var subQ1=sQuery(id+"F0.wireOp",EDGE,"E47.0.1.0");var subQ2=makeQuery(id+"F0.imprint","INTERSECT",VERTEX,{"derivedFrom":[subQ1,subQ0]});Q52=makeQuery(id+"F0.imprint","IMPRINT",FACE,{"disambiguationData":[TD([[makeQuery(id+"F0.imprint","IMPRINT",EDGE,{"disambiguationData":[TD([[subQ2,1.0]])],"derivedFrom":subQ1}),1.0]])]});}
            var Q53;
            {var subQ0=sQuery(id+"F0.wireOp",EDGE,"E120.trimOffspring");var subQ1=sQuery(id+"F0.wireOp",EDGE,"E41");var subQ2=makeQuery(id+"F0.imprint","INTERSECT",VERTEX,{"derivedFrom":[subQ1,subQ0]});Q53=makeQuery(id+"F0.imprint","IMPRINT",FACE,{"disambiguationData":[TD([[makeQuery(id+"F0.imprint","IMPRINT",EDGE,{"disambiguationData":[TD([[subQ2,-1.0]])],"derivedFrom":subQ1}),-1.0]])]});}
            var Q54;
            {var subQ0=sQuery(id+"F0.wireOp",EDGE,"E188.trimOffspring");var subQ1=sQuery(id+"F0.wireOp",EDGE,"E106.trimOffspring");var subQ2=makeQuery(id+"F0.imprint","INTERSECT",VERTEX,{"derivedFrom":[subQ1,subQ0]});Q54=makeQuery(id+"F0.imprint","IMPRINT",FACE,{"disambiguationData":[TD([[makeQuery(id+"F0.imprint","IMPRINT",EDGE,{"disambiguationData":[TD([[subQ2,-1.0]])],"derivedFrom":subQ1}),1.0]])]});}
            var Q55;
            {var subQ0=sQuery(id+"F0.wireOp",EDGE,"E106.trimOffspring");var subQ1=sQuery(id+"F0.wireOp",EDGE,"E41");var subQ2=makeQuery(id+"F0.imprint","INTERSECT",VERTEX,{"derivedFrom":[subQ1,subQ0]});Q55=makeQuery(id+"F0.imprint","IMPRINT",FACE,{"disambiguationData":[TD([[makeQuery(id+"F0.imprint","IMPRINT",EDGE,{"disambiguationData":[TD([[subQ2,-1.0]])],"derivedFrom":subQ1}),-1.0]])]});}
            var Q56;
            {var subQ0=sQuery(id+"F0.wireOp",EDGE,"E112.trimOffspring");var subQ1=sQuery(id+"F0.wireOp",EDGE,"E41");var subQ2=makeQuery(id+"F0.imprint","INTERSECT",VERTEX,{"derivedFrom":[subQ1,subQ0]});Q56=makeQuery(id+"F0.imprint","IMPRINT",FACE,{"disambiguationData":[TD([[makeQuery(id+"F0.imprint","IMPRINT",EDGE,{"disambiguationData":[TD([[subQ2,-1.0]])],"derivedFrom":subQ1}),-1.0]])]});}
            var Q57;
            {var subQ0=sQuery(id+"F0.wireOp",EDGE,"E124.trimOffspring");var subQ1=sQuery(id+"F0.wireOp",EDGE,"E90");var subQ2=makeQuery(id+"F0.imprint","INTERSECT",VERTEX,{"derivedFrom":[subQ1,subQ0]});Q57=makeQuery(id+"F0.imprint","IMPRINT",FACE,{"disambiguationData":[TD([[makeQuery(id+"F0.imprint","IMPRINT",EDGE,{"disambiguationData":[TD([[subQ2,-1.0]])],"derivedFrom":subQ1}),-1.0]])]});}
            extrude(context, id + "F4", {"entities" : qUnion([Q0, Q1, Q2, Q3, Q4, Q5, Q6, Q7, Q8, Q9, Q10, Q11, Q12, Q13, Q14, Q15, Q16, Q17, Q18, Q19, Q20, Q21, Q22, Q23, Q24, Q25, Q26, Q27, Q28, Q29, Q30, Q31, Q32, Q33, Q34, Q35, Q36, Q37, Q38, Q39, Q40, Q41, Q42, Q43, Q44, Q45, Q46, Q47, Q48, Q49, Q50, Q51, Q52, Q53, Q54, Q55, Q56, Q57]), "depth" : 25.4 * mm});
        }
        {
            var Q0;
            Q0=makeQuery(id+"F2.opExtrude","CAP_FACE",FACE,{"disambiguationData":[OSD([sQuery(id+"F0.wireOp",EDGE,"E0.bottom"),sQuery(id+"F0.wireOp",EDGE,"E0.right"),sQuery(id+"F0.wireOp",EDGE,"E1.bottom"),sQuery(id+"F0.wireOp",EDGE,"E1.left"),sQuery(id+"F0.wireOp",EDGE,"E2.bottom"),sQuery(id+"F0.wireOp",EDGE,"E3.left"),sQuery(id+"F0.wireOp",EDGE,"E7.0"),sQuery(id+"F0.wireOp",EDGE,"E10.trimOffspring"),sQuery(id+"F0.wireOp",EDGE,"E11.trimOffspring"),sQuery(id+"F0.wireOp",EDGE,"E13.0"),sQuery(id+"F0.wireOp",EDGE,"E14.0"),sQuery(id+"F0.wireOp",EDGE,"E17.trimOffspring"),sQuery(id+"F0.wireOp",EDGE,"E18.trimOffspring"),sQuery(id+"F0.wireOp",EDGE,"E19.0"),sQuery(id+"F0.wireOp",EDGE,"E20.trimOffspring"),sQuery(id+"F0.wireOp",EDGE,"E22.trimOffspring"),sQuery(id+"F0.wireOp",EDGE,"E23.trimOffspring"),sQuery(id+"F0.wireOp",EDGE,"E24.trimOffspring"),sQuery(id+"F0.wireOp",EDGE,"E27.0"),sQuery(id+"F0.wireOp",EDGE,"E28.trimOffspring"),sQuery(id+"F0.wireOp",EDGE,"E29"),sQuery(id+"F0.wireOp",EDGE,"E30"),sQuery(id+"F0.wireOp",EDGE,"E31"),sQuery(id+"F0.wireOp",EDGE,"E32")])],"isStart":false});
            var sketch = newSketch(context, id + "F5", { "sketchPlane" : qUnion([Q0])});
            skLineSegment(sketch, "E192", {"start": v(5697.15, 7273.06) * mm, "end": v(5697.15, 7277.55) * mm});
            skLineSegment(sketch, "E193", {"start": v(5692.66, 7277.55) * mm, "end": v(5697.15, 7277.55) * mm});
            skSolve(sketch);
        }
        {
            var Q0;
            Q0=qCreatedBy(makeId("Top.planeOp"),FACE);
            var sketch = newSketch(context, id + "F6", { "sketchPlane" : qUnion([Q0])});
            skLineSegment(sketch, "E194.bottom", {"start": v(-2132.67, 7026.12) * mm, "end": v(-1992.97, 7026.12) * mm});
            skLineSegment(sketch, "E194.top", {"start": v(-2132.67, 282.42) * mm, "end": v(-1992.97, 282.42) * mm});
            skLineSegment(sketch, "E194.left", {"start": v(-2132.67, 7026.12) * mm, "end": v(-2132.67, 282.42) * mm});
            skLineSegment(sketch, "E194.right", {"start": v(-1992.97, 7026.12) * mm, "end": v(-1992.97, 282.42) * mm});
            skSolve(sketch);
        }
        {
            var Q0;
            Q0 = qSketchRegion(id + "F6", true);
            extrude(context, id + "F7", {"entities" : qUnion([Q0]), "depth" : 25.4 * mm});
        }
        {
            var Q0;
            Q0=qCreatedBy(makeId("Top.planeOp"),FACE);
            var sketch = newSketch(context, id + "F8", { "sketchPlane" : qUnion([Q0])});
            skLineSegment(sketch, "E195.bottom", {"start": v(-3198.42, 3513.5) * mm, "end": v(-3338.12, 3513.5) * mm});
            skLineSegment(sketch, "E195.top", {"start": v(-3198.42, 894.13) * mm, "end": v(-3338.12, 894.13) * mm});
            skLineSegment(sketch, "E195.left", {"start": v(-3198.42, 3513.5) * mm, "end": v(-3198.42, 894.13) * mm});
            skLineSegment(sketch, "E195.right", {"start": v(-3338.12, 3513.5) * mm, "end": v(-3338.12, 894.13) * mm});
            skSolve(sketch);
        }
        {
            var Q0;
            Q0 = qSketchRegion(id + "F8", true);
            extrude(context, id + "F9", {"entities" : qUnion([Q0]), "depth" : 25.4 * mm});
        }
        {
            var Q0;
            Q0=qCreatedBy(makeId("Front.planeOp"),FACE);
            var sketch = newSketch(context, id + "F10", { "sketchPlane" : qUnion([Q0])});
            skLineSegment(sketch, "E196.bottom", {"start": v(-4978.27, -1438.89) * mm, "end": v(-4838.57, -1438.89) * mm});
            skLineSegment(sketch, "E196.top", {"start": v(-4978.27, -524.49) * mm, "end": v(-4838.57, -524.49) * mm});
            skLineSegment(sketch, "E196.left", {"start": v(-4978.27, -1438.89) * mm, "end": v(-4978.27, -524.49) * mm});
            skLineSegment(sketch, "E196.right", {"start": v(-4838.57, -1438.89) * mm, "end": v(-4838.57, -524.49) * mm});
            skLineSegment(sketch, "E197.top", {"start": v(-4978.27, -1413.49) * mm, "end": v(-4838.57, -1413.49) * mm});
            skLineSegment(sketch, "E197.left", {"start": v(-4978.27, -1438.89) * mm, "end": v(-4978.27, -1413.49) * mm});
            skLineSegment(sketch, "E197.right", {"start": v(-4838.57, -1438.89) * mm, "end": v(-4838.57, -1413.49) * mm});
            skLineSegment(sketch, "E198.bottom", {"start": v(-4908.42, -1413.49) * mm, "end": v(-4883.02, -1413.49) * mm});
            skLineSegment(sketch, "E198.top", {"start": v(-4908.42, -1362.69) * mm, "end": v(-4883.02, -1362.69) * mm});
            skLineSegment(sketch, "E198.left", {"start": v(-4908.42, -1413.49) * mm, "end": v(-4908.42, -1362.69) * mm});
            skLineSegment(sketch, "E198.right", {"start": v(-4883.02, -1413.49) * mm, "end": v(-4883.02, -1362.69) * mm});
            skLineSegment(sketch, "E199.bottom", {"start": v(-4908.42, -1413.49) * mm, "end": v(-4933.82, -1413.49) * mm});
            skLineSegment(sketch, "E199.top", {"start": v(-4908.42, -1362.69) * mm, "end": v(-4933.82, -1362.69) * mm});
            skLineSegment(sketch, "E199.right", {"start": v(-4933.82, -1413.49) * mm, "end": v(-4933.82, -1362.69) * mm});
            skCircle(sketch, "E200", {"center": v(-4908.42, -1273.79) * mm, "radius": 1.59 * mm});
            skCircle(sketch, "E201.0.1.0", {"center": v(-4908.42, -1184.89) * mm, "radius": 1.59 * mm});
            skCircle(sketch, "E201.0.2.0", {"center": v(-4908.42, -1095.99) * mm, "radius": 1.59 * mm});
            skCircle(sketch, "E201.0.3.0", {"center": v(-4908.42, -1007.09) * mm, "radius": 1.59 * mm});
            skCircle(sketch, "E201.0.4.0", {"center": v(-4908.42, -918.19) * mm, "radius": 1.59 * mm});
            skCircle(sketch, "E201.0.5.0", {"center": v(-4908.42, -829.29) * mm, "radius": 1.59 * mm});
            skCircle(sketch, "E201.0.6.0", {"center": v(-4908.42, -740.39) * mm, "radius": 1.59 * mm});
            skCircle(sketch, "E201.0.7.0", {"center": v(-4908.42, -651.49) * mm, "radius": 1.59 * mm});
            skCircle(sketch, "E201.0.8.0", {"center": v(-4908.42, -562.59) * mm, "radius": 1.59 * mm});
            skLineSegment(sketch, "E202.bottom", {"start": v(-6095.78, -1057.94) * mm, "end": v(-5956.08, -1057.94) * mm});
            skLineSegment(sketch, "E202.top", {"start": v(-6095.78, -143.54) * mm, "end": v(-5956.08, -143.54) * mm});
            skLineSegment(sketch, "E202.left", {"start": v(-6095.78, -1057.94) * mm, "end": v(-6095.78, -143.54) * mm});
            skLineSegment(sketch, "E202.right", {"start": v(-5956.08, -1057.94) * mm, "end": v(-5956.08, -143.54) * mm});
            skLineSegment(sketch, "E203.top", {"start": v(-6095.78, -1032.54) * mm, "end": v(-5956.08, -1032.54) * mm});
            skLineSegment(sketch, "E203.left", {"start": v(-6095.78, -1057.94) * mm, "end": v(-6095.78, -1032.54) * mm});
            skLineSegment(sketch, "E203.right", {"start": v(-5956.08, -1057.94) * mm, "end": v(-5956.08, -1032.54) * mm});
            skLineSegment(sketch, "E204.bottom", {"start": v(-6025.93, -1032.54) * mm, "end": v(-6000.53, -1032.54) * mm});
            skLineSegment(sketch, "E204.top", {"start": v(-6025.93, -981.74) * mm, "end": v(-6000.53, -981.74) * mm});
            skLineSegment(sketch, "E204.left", {"start": v(-6025.93, -1032.54) * mm, "end": v(-6025.93, -981.74) * mm});
            skLineSegment(sketch, "E204.right", {"start": v(-6000.53, -1032.54) * mm, "end": v(-6000.53, -981.74) * mm});
            skLineSegment(sketch, "E205.bottom", {"start": v(-6025.93, -1032.54) * mm, "end": v(-6051.33, -1032.54) * mm});
            skLineSegment(sketch, "E205.top", {"start": v(-6025.93, -981.74) * mm, "end": v(-6051.33, -981.74) * mm});
            skLineSegment(sketch, "E205.right", {"start": v(-6051.33, -1032.54) * mm, "end": v(-6051.33, -981.74) * mm});
            skCircle(sketch, "E206", {"center": v(-6025.93, -892.84) * mm, "radius": 1.59 * mm});
            skCircle(sketch, "E207.0.1.0", {"center": v(-6025.93, -803.94) * mm, "radius": 1.59 * mm});
            skCircle(sketch, "E207.0.2.0", {"center": v(-6025.93, -715.04) * mm, "radius": 1.59 * mm});
            skCircle(sketch, "E207.0.3.0", {"center": v(-6025.93, -626.14) * mm, "radius": 1.59 * mm});
            skCircle(sketch, "E207.0.4.0", {"center": v(-6025.93, -537.24) * mm, "radius": 1.59 * mm});
            skCircle(sketch, "E207.0.5.0", {"center": v(-6025.93, -448.34) * mm, "radius": 1.59 * mm});
            skCircle(sketch, "E207.0.6.0", {"center": v(-6025.93, -359.44) * mm, "radius": 1.59 * mm});
            skCircle(sketch, "E207.0.7.0", {"center": v(-6025.93, -270.54) * mm, "radius": 1.59 * mm});
            skCircle(sketch, "E207.0.8.0", {"center": v(-6025.93, -181.64) * mm, "radius": 1.59 * mm});
            skLineSegment(sketch, "E208.bottom", {"start": v(-5537.71, -478.04) * mm, "end": v(-5398.01, -478.04) * mm});
            skLineSegment(sketch, "E208.top", {"start": v(-5537.71, 436.36) * mm, "end": v(-5398.01, 436.36) * mm});
            skLineSegment(sketch, "E208.left", {"start": v(-5537.71, -478.04) * mm, "end": v(-5537.71, 436.36) * mm});
            skLineSegment(sketch, "E208.right", {"start": v(-5398.01, -478.04) * mm, "end": v(-5398.01, 436.36) * mm});
            skLineSegment(sketch, "E209.top", {"start": v(-5537.71, -452.64) * mm, "end": v(-5398.01, -452.64) * mm});
            skLineSegment(sketch, "E209.left", {"start": v(-5537.71, -478.04) * mm, "end": v(-5537.71, -452.64) * mm});
            skLineSegment(sketch, "E209.right", {"start": v(-5398.01, -478.04) * mm, "end": v(-5398.01, -452.64) * mm});
            skLineSegment(sketch, "E210", {"start": v(-5467.86, -452.64) * mm, "end": v(-5467.86, 436.36) * mm});
            skLineSegment(sketch, "E211.bottom", {"start": v(-5467.86, -452.64) * mm, "end": v(-5442.46, -452.64) * mm});
            skLineSegment(sketch, "E211.top", {"start": v(-5467.86, -401.84) * mm, "end": v(-5442.46, -401.84) * mm});
            skLineSegment(sketch, "E211.left", {"start": v(-5467.86, -452.64) * mm, "end": v(-5467.86, -401.84) * mm});
            skLineSegment(sketch, "E211.right", {"start": v(-5442.46, -452.64) * mm, "end": v(-5442.46, -401.84) * mm});
            skLineSegment(sketch, "E212.bottom", {"start": v(-5467.86, -452.64) * mm, "end": v(-5493.26, -452.64) * mm});
            skLineSegment(sketch, "E212.top", {"start": v(-5467.86, -401.84) * mm, "end": v(-5493.26, -401.84) * mm});
            skLineSegment(sketch, "E212.right", {"start": v(-5493.26, -452.64) * mm, "end": v(-5493.26, -401.84) * mm});
            skLineSegment(sketch, "E213", {"start": v(-5467.86, -312.94) * mm, "end": v(-5275.93, -312.94) * mm});
            skCircle(sketch, "E214", {"center": v(-5467.86, -312.94) * mm, "radius": 1.59 * mm});
            skCircle(sketch, "E215.0.1.0", {"center": v(-5467.86, -224.04) * mm, "radius": 1.59 * mm});
            skCircle(sketch, "E215.0.2.0", {"center": v(-5467.86, -135.14) * mm, "radius": 1.59 * mm});
            skCircle(sketch, "E215.0.3.0", {"center": v(-5467.86, -46.24) * mm, "radius": 1.59 * mm});
            skCircle(sketch, "E215.0.4.0", {"center": v(-5467.86, 42.66) * mm, "radius": 1.59 * mm});
            skCircle(sketch, "E215.0.5.0", {"center": v(-5467.86, 131.56) * mm, "radius": 1.59 * mm});
            skCircle(sketch, "E215.0.6.0", {"center": v(-5467.86, 220.46) * mm, "radius": 1.59 * mm});
            skCircle(sketch, "E215.0.7.0", {"center": v(-5467.86, 309.36) * mm, "radius": 1.59 * mm});
            skCircle(sketch, "E215.0.8.0", {"center": v(-5467.86, 398.26) * mm, "radius": 1.59 * mm});
            skLineSegment(sketch, "E215.direction1", {"start": v(-5467.86, -312.94) * mm, "end": v(-5442.46, -312.94) * mm, "construction": true});
            skLineSegment(sketch, "E215.direction2", {"start": v(-5467.86, -312.94) * mm, "end": v(-5467.86, -224.04) * mm, "construction": true});
            skLineSegment(sketch, "E216.bottom", {"start": v(-4933.82, -1362.69) * mm, "end": v(-4883.02, -1362.69) * mm});
            skLineSegment(sketch, "E216.top", {"start": v(-4933.82, -1362.69) * mm, "end": v(-4883.02, -1362.69) * mm});
            skLineSegment(sketch, "E216.left", {"start": v(-4933.82, -1362.69) * mm, "end": v(-4933.82, -1362.69) * mm});
            skLineSegment(sketch, "E216.right", {"start": v(-4883.02, -1362.69) * mm, "end": v(-4883.02, -1362.69) * mm});
            skLineSegment(sketch, "E217.bottom", {"start": v(-4933.82, -1362.69) * mm, "end": v(-4884.14, -1362.69) * mm});
            skLineSegment(sketch, "E217.top", {"start": v(-4933.82, -524.49) * mm, "end": v(-4884.14, -524.49) * mm});
            skLineSegment(sketch, "E217.left", {"start": v(-4933.82, -1362.69) * mm, "end": v(-4933.82, -524.49) * mm});
            skLineSegment(sketch, "E217.right", {"start": v(-4884.14, -1362.69) * mm, "end": v(-4884.14, -524.49) * mm});
            skSolve(sketch);
        }
        {
            var Q0;
            Q0=makeQuery(id+"F10.imprint","IMPRINT",FACE,{"disambiguationData":[TD([[makeQuery(id+"F10.imprint","IMPRINT",EDGE,{"derivedFrom":sQuery(id+"F10.wireOp",EDGE,"E201.0.8.0")}),1.0]])]});
            var Q1;
            Q1=makeQuery(id+"F10.imprint","IMPRINT",FACE,{"disambiguationData":[TD([[makeQuery(id+"F10.imprint","IMPRINT",EDGE,{"derivedFrom":sQuery(id+"F10.wireOp",EDGE,"E201.0.7.0")}),1.0]])]});
            var Q2;
            Q2=makeQuery(id+"F10.imprint","IMPRINT",FACE,{"disambiguationData":[TD([[makeQuery(id+"F10.imprint","IMPRINT",EDGE,{"derivedFrom":sQuery(id+"F10.wireOp",EDGE,"E201.0.6.0")}),1.0]])]});
            var Q3;
            Q3=makeQuery(id+"F10.imprint","IMPRINT",FACE,{"disambiguationData":[TD([[makeQuery(id+"F10.imprint","IMPRINT",EDGE,{"derivedFrom":sQuery(id+"F10.wireOp",EDGE,"E201.0.5.0")}),1.0]])]});
            var Q4;
            Q4=makeQuery(id+"F10.imprint","IMPRINT",FACE,{"disambiguationData":[TD([[makeQuery(id+"F10.imprint","IMPRINT",EDGE,{"derivedFrom":sQuery(id+"F10.wireOp",EDGE,"E201.0.4.0")}),1.0]])]});
            var Q5;
            Q5=makeQuery(id+"F10.imprint","IMPRINT",FACE,{"disambiguationData":[TD([[makeQuery(id+"F10.imprint","IMPRINT",EDGE,{"derivedFrom":sQuery(id+"F10.wireOp",EDGE,"E201.0.3.0")}),1.0]])]});
            var Q6;
            Q6=makeQuery(id+"F10.imprint","IMPRINT",FACE,{"disambiguationData":[TD([[makeQuery(id+"F10.imprint","IMPRINT",EDGE,{"derivedFrom":sQuery(id+"F10.wireOp",EDGE,"E201.0.2.0")}),1.0]])]});
            var Q7;
            Q7=makeQuery(id+"F10.imprint","IMPRINT",FACE,{"disambiguationData":[TD([[makeQuery(id+"F10.imprint","IMPRINT",EDGE,{"derivedFrom":sQuery(id+"F10.wireOp",EDGE,"E201.0.1.0")}),1.0]])]});
            var Q8;
            Q8=makeQuery(id+"F10.imprint","IMPRINT",FACE,{"disambiguationData":[TD([[makeQuery(id+"F10.imprint","IMPRINT",EDGE,{"derivedFrom":sQuery(id+"F10.wireOp",EDGE,"E200")}),1.0]])]});
            var Q9;
            Q9=makeQuery(id+"F10.imprint","IMPRINT",FACE,{"disambiguationData":[TD([[makeQuery(id+"F10.imprint","IMPRINT",EDGE,{"derivedFrom":sQuery(id+"F10.wireOp",EDGE,"E198.bottom")}),1.0]])]});
            var Q10;
            Q10=makeQuery(id+"F10.imprint","IMPRINT",FACE,{"disambiguationData":[TD([[makeQuery(id+"F10.imprint","IMPRINT",EDGE,{"derivedFrom":sQuery(id+"F10.wireOp",EDGE,"E199.bottom")}),-1.0]])]});
            var Q11;
            Q11=makeQuery(id+"F10.imprint","IMPRINT",FACE,{"disambiguationData":[TD([[makeQuery(id+"F10.imprint","IMPRINT",EDGE,{"derivedFrom":sQuery(id+"F10.wireOp",EDGE,"E196.bottom")}),1.0]])]});
            extrude(context, id + "F11", {"entities" : qUnion([Q0, Q1, Q2, Q3, Q4, Q5, Q6, Q7, Q8, Q9, Q10, Q11]), "depth" : 6959.6 * mm});
        }
        {
            var Q0;
            Q0=makeQuery(id+"F10.imprint","IMPRINT",FACE,{"disambiguationData":[TD([[makeQuery(id+"F10.imprint","IMPRINT",EDGE,{"derivedFrom":sQuery(id+"F10.wireOp",EDGE,"E202.bottom")}),1.0]])]});
            var Q1;
            Q1=makeQuery(id+"F10.imprint","IMPRINT",FACE,{"disambiguationData":[TD([[makeQuery(id+"F10.imprint","IMPRINT",EDGE,{"derivedFrom":sQuery(id+"F10.wireOp",EDGE,"E204.bottom")}),1.0]])]});
            var Q2;
            Q2=makeQuery(id+"F10.imprint","IMPRINT",FACE,{"disambiguationData":[TD([[makeQuery(id+"F10.imprint","IMPRINT",EDGE,{"derivedFrom":sQuery(id+"F10.wireOp",EDGE,"E205.bottom")}),-1.0]])]});
            var Q3;
            Q3=makeQuery(id+"F10.imprint","IMPRINT",FACE,{"disambiguationData":[TD([[makeQuery(id+"F10.imprint","IMPRINT",EDGE,{"derivedFrom":sQuery(id+"F10.wireOp",EDGE,"E207.0.1.0")}),1.0]])]});
            var Q4;
            Q4=makeQuery(id+"F10.imprint","IMPRINT",FACE,{"disambiguationData":[TD([[makeQuery(id+"F10.imprint","IMPRINT",EDGE,{"derivedFrom":sQuery(id+"F10.wireOp",EDGE,"E207.0.3.0")}),1.0]])]});
            var Q5;
            Q5=makeQuery(id+"F10.imprint","IMPRINT",FACE,{"disambiguationData":[TD([[makeQuery(id+"F10.imprint","IMPRINT",EDGE,{"derivedFrom":sQuery(id+"F10.wireOp",EDGE,"E207.0.2.0")}),1.0]])]});
            var Q6;
            Q6=makeQuery(id+"F10.imprint","IMPRINT",FACE,{"disambiguationData":[TD([[makeQuery(id+"F10.imprint","IMPRINT",EDGE,{"derivedFrom":sQuery(id+"F10.wireOp",EDGE,"E206")}),1.0]])]});
            var Q7;
            Q7=makeQuery(id+"F10.imprint","IMPRINT",FACE,{"disambiguationData":[TD([[makeQuery(id+"F10.imprint","IMPRINT",EDGE,{"derivedFrom":sQuery(id+"F10.wireOp",EDGE,"E207.0.7.0")}),1.0]])]});
            var Q8;
            Q8=makeQuery(id+"F10.imprint","IMPRINT",FACE,{"disambiguationData":[TD([[makeQuery(id+"F10.imprint","IMPRINT",EDGE,{"derivedFrom":sQuery(id+"F10.wireOp",EDGE,"E207.0.4.0")}),1.0]])]});
            var Q9;
            Q9=makeQuery(id+"F10.imprint","IMPRINT",FACE,{"disambiguationData":[TD([[makeQuery(id+"F10.imprint","IMPRINT",EDGE,{"derivedFrom":sQuery(id+"F10.wireOp",EDGE,"E207.0.6.0")}),1.0]])]});
            var Q10;
            Q10=makeQuery(id+"F10.imprint","IMPRINT",FACE,{"disambiguationData":[TD([[makeQuery(id+"F10.imprint","IMPRINT",EDGE,{"derivedFrom":sQuery(id+"F10.wireOp",EDGE,"E207.0.5.0")}),1.0]])]});
            var Q11;
            Q11=makeQuery(id+"F10.imprint","IMPRINT",FACE,{"disambiguationData":[TD([[makeQuery(id+"F10.imprint","IMPRINT",EDGE,{"derivedFrom":sQuery(id+"F10.wireOp",EDGE,"E207.0.8.0")}),1.0]])]});
            var Q12;
            Q12=makeQuery(id+"F11.opExtrude","CAP_FACE",FACE,{"disambiguationData":[OSD([sQuery(id+"F10.wireOp",EDGE,"E201.0.8.0")])],"isStart":false});
            extrude(context, id + "F12", {"entities" : qUnion([Q0, Q1, Q2, Q3, Q4, Q5, Q6, Q7, Q8, Q9, Q10, Q11, Q12]), "operationType" : NewBodyOperationType.ADD, "depth" : 5881.76 * mm});
        }
        {
            var Q0;
            Q0=makeQuery(id+"F10.imprint","IMPRINT",FACE,{"disambiguationData":[TD([[makeQuery(id+"F10.imprint","IMPRINT",EDGE,{"derivedFrom":sQuery(id+"F10.wireOp",EDGE,"E202.top")}),-1.0]])]});
            extrude(context, id + "F13", {"entities" : qUnion([Q0]), "depth" : 25.4 * mm});
        }
        {
            var Q0;
            Q0=makeQuery(id+"F12.opExtrude","SWEPT_BODY",BODY,{"disambiguationData":[OSD([sQuery(id+"F10.wireOp",EDGE,"E202.bottom"),sQuery(id+"F10.wireOp",EDGE,"E203.top"),sQuery(id+"F10.wireOp",EDGE,"E203.left"),sQuery(id+"F10.wireOp",EDGE,"E203.right"),sQuery(id+"F10.wireOp",EDGE,"E204.top"),sQuery(id+"F10.wireOp",EDGE,"E204.right"),sQuery(id+"F10.wireOp",EDGE,"E205.top"),sQuery(id+"F10.wireOp",EDGE,"E205.right")])]});
            var Q1;
            Q1=makeQuery(id+"F12.opExtrude","SWEPT_BODY",BODY,{"disambiguationData":[OSD([sQuery(id+"F10.wireOp",EDGE,"E207.0.7.0")])]});
            var Q2;
            Q2=makeQuery(id+"F12.opExtrude","SWEPT_BODY",BODY,{"disambiguationData":[OSD([sQuery(id+"F10.wireOp",EDGE,"E207.0.6.0")])]});
            var Q3;
            Q3=makeQuery(id+"F12.opExtrude","SWEPT_BODY",BODY,{"disambiguationData":[OSD([sQuery(id+"F10.wireOp",EDGE,"E207.0.3.0")])]});
            var Q4;
            Q4=makeQuery(id+"F12.opExtrude","SWEPT_BODY",BODY,{"disambiguationData":[OSD([sQuery(id+"F10.wireOp",EDGE,"E206")])]});
            var Q5;
            Q5=makeQuery(id+"F12.opExtrude","SWEPT_BODY",BODY,{"disambiguationData":[OSD([sQuery(id+"F10.wireOp",EDGE,"E207.0.8.0")])]});
            var Q6;
            Q6=makeQuery(id+"F12.opExtrude","SWEPT_BODY",BODY,{"disambiguationData":[OSD([sQuery(id+"F10.wireOp",EDGE,"E207.0.5.0")])]});
            var Q7;
            Q7=makeQuery(id+"F12.opExtrude","SWEPT_BODY",BODY,{"disambiguationData":[OSD([sQuery(id+"F10.wireOp",EDGE,"E207.0.4.0")])]});
            var Q8;
            Q8=makeQuery(id+"F13.opExtrude","SWEPT_BODY",BODY,{"disambiguationData":[OSD([sQuery(id+"F10.wireOp",EDGE,"E202.top"),sQuery(id+"F10.wireOp",EDGE,"E202.left"),sQuery(id+"F10.wireOp",EDGE,"E202.right"),sQuery(id+"F10.wireOp",EDGE,"E203.top"),sQuery(id+"F10.wireOp",EDGE,"E204.top"),sQuery(id+"F10.wireOp",EDGE,"E204.right"),sQuery(id+"F10.wireOp",EDGE,"E205.top"),sQuery(id+"F10.wireOp",EDGE,"E205.right"),sQuery(id+"F10.wireOp",EDGE,"E206"),sQuery(id+"F10.wireOp",EDGE,"E207.0.1.0"),sQuery(id+"F10.wireOp",EDGE,"E207.0.2.0"),sQuery(id+"F10.wireOp",EDGE,"E207.0.3.0"),sQuery(id+"F10.wireOp",EDGE,"E207.0.4.0"),sQuery(id+"F10.wireOp",EDGE,"E207.0.5.0"),sQuery(id+"F10.wireOp",EDGE,"E207.0.6.0"),sQuery(id+"F10.wireOp",EDGE,"E207.0.7.0"),sQuery(id+"F10.wireOp",EDGE,"E207.0.8.0")])]});
            var Q9;
            Q9=makeQuery(id+"F12.opExtrude","SWEPT_BODY",BODY,{"disambiguationData":[OSD([sQuery(id+"F10.wireOp",EDGE,"E207.0.2.0")])]});
            var Q10;
            Q10=makeQuery(id+"F12.opExtrude","SWEPT_BODY",BODY,{"disambiguationData":[OSD([sQuery(id+"F10.wireOp",EDGE,"E207.0.1.0")])]});
            booleanBodies(context, id + "F14", {"operationType" : BooleanOperationType.UNION, "tools" : qUnion([Q0, Q1, Q2, Q3, Q4, Q5, Q6, Q7, Q8, Q9, Q10])});
        }
        {
            var Q0;
            {var subQ1=sQuery(id+"F10.wireOp",EDGE,"E196.right");Q0=makeQuery(id+"F10.imprint","IMPRINT",FACE,{"disambiguationData":[TD([[makeQuery(id+"F10.imprint","IMPRINT",EDGE,{"derivedFrom":subQ1}),1.0]])]});}
            var Q1;
            Q1=makeQuery(id+"F10.imprint","IMPRINT",FACE,{"disambiguationData":[TD([[makeQuery(id+"F10.imprint","IMPRINT",EDGE,{"derivedFrom":sQuery(id+"F10.wireOp",EDGE,"E200")}),-1.0]])]});
            var Q2;
            {var subQ2=sQuery(id+"F10.wireOp",EDGE,"E196.left");Q2=makeQuery(id+"F10.imprint","IMPRINT",FACE,{"disambiguationData":[TD([[makeQuery(id+"F10.imprint","IMPRINT",EDGE,{"derivedFrom":subQ2}),-1.0]])]});}
            extrude(context, id + "F15", {"entities" : qUnion([Q0, Q1, Q2]), "depth" : 25.4 * mm});
        }
        {
            var Q0;
            Q0=makeQuery(id+"F7.opExtrude","SWEPT_BODY",BODY,{"disambiguationData":[OSD([sQuery(id+"F6.wireOp",EDGE,"E194.bottom"),sQuery(id+"F6.wireOp",EDGE,"E194.top"),sQuery(id+"F6.wireOp",EDGE,"E194.left"),sQuery(id+"F6.wireOp",EDGE,"E194.right")])]});
            deleteBodies(context, id + "F16", {"entities" : qUnion([Q0])});
        }
        {
            var Q0;
            Q0=makeQuery(id+"F9.opExtrude","SWEPT_BODY",BODY,{"disambiguationData":[OSD([sQuery(id+"F8.wireOp",EDGE,"E195.bottom"),sQuery(id+"F8.wireOp",EDGE,"E195.top"),sQuery(id+"F8.wireOp",EDGE,"E195.left"),sQuery(id+"F8.wireOp",EDGE,"E195.right")])]});
            deleteBodies(context, id + "F17", {"entities" : qUnion([Q0])});
        }
    });
